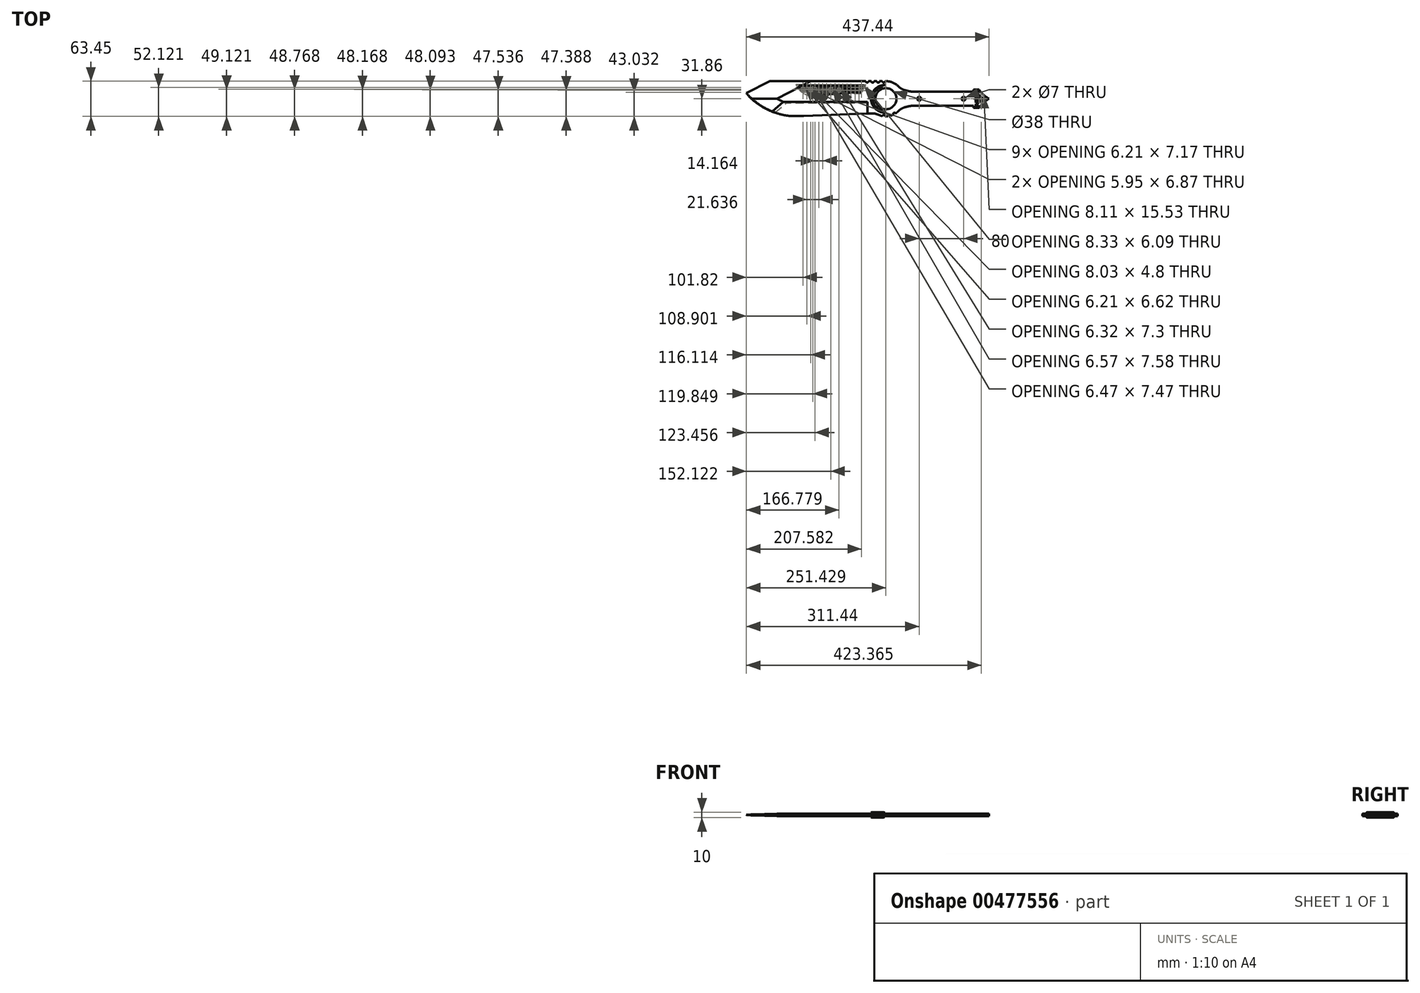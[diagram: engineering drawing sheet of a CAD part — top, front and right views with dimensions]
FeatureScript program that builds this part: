
annotation { "Feature Type Name" : "Feature", "Feature Type Description" : "" }
export const myFeature = defineFeature(function(context is Context, id is Id, definition is map)
    precondition{}
    {
        {
            var Q0;
            Q0=qCreatedBy(makeId("Top.planeOp"),FACE);
            var sketch = newSketch(context, id + "F0", { "sketchPlane" : qUnion([Q0])});
            skLineSegment(sketch, "E0", {"start": v(57.87, 16.75) * mm, "end": v(67.87, 16.75) * mm});
            skLineSegment(sketch, "E1", {"start": v(57.87, 16.75) * mm, "end": v(57.87, 12.5) * mm});
            skLineSegment(sketch, "E2", {"start": v(57.87, 12.5) * mm, "end": v(-46.76, 12.5) * mm});
            skArc(sketch, "E3", {"start": v(-67.13, 15.9) * mm, "mid": v(-57.09, 13.35) * mm, "end": v(-46.76, 12.5) * mm});
            skArc(sketch, "E4", {"start": v(-77.6, 22.42) * mm, "mid": v(-86.65, 28.75) * mm, "end": v(-97.34, 31.6) * mm});
            skCircle(sketch, "E5", {"center": v(-100.01, 0) * mm, "radius": 19 * mm});
            skLineSegment(sketch, "E6.MirrorCS", {"start": v(57.87, -16.75) * mm, "end": v(67.87, -16.75) * mm});
            skLineSegment(sketch, "E7.MirrorCS", {"start": v(57.87, -12.5) * mm, "end": v(57.87, -16.75) * mm});
            skLineSegment(sketch, "E8.MirrorCS", {"start": v(57.87, -12.5) * mm, "end": v(-46.76, -12.5) * mm});
            skArc(sketch, "E9.MirrorCS", {"start": v(-67.13, -15.9) * mm, "mid": v(-57.09, -13.35) * mm, "end": v(-46.76, -12.5) * mm});
            skArc(sketch, "E10.MirrorCS", {"start": v(-77.6, -22.42) * mm, "mid": v(-87.33, -29.06) * mm, "end": v(-98.81, -31.68) * mm});
            skPoint(sketch, "E11.visualSharp", {"position": v(-125.37, 19.03) * mm});
            skPoint(sketch, "E12.visualSharp", {"position": v(-125.37, -19.03) * mm});
            skPoint(sketch, "E13.visualSharp", {"position": v(-74.65, 19.03) * mm});
            skArc(sketch, "E13.filletArc", {"start": v(-77.6, 22.42) * mm, "mid": v(-72.73, 18.56) * mm, "end": v(-67.13, 15.9) * mm});
            skPoint(sketch, "E14.visualSharp", {"position": v(-74.65, -19.03) * mm});
            skArc(sketch, "E14.filletArc", {"start": v(-67.13, -15.9) * mm, "mid": v(-72.73, -18.56) * mm, "end": v(-77.6, -22.42) * mm});
            skLineSegment(sketch, "E15", {"start": v(-367.34, 31.6) * mm, "end": v(-97.34, 31.6) * mm});
            skArc(sketch, "E16", {"start": v(-112.05, -29.48) * mm, "mid": v(-105.6, -31.54) * mm, "end": v(-98.81, -31.68) * mm});
            skPoint(sketch, "E17.startSnap0", {"position": v(-107.38, -31.17) * mm});
            skPoint(sketch, "E18.visualSharp", {"position": v(-117.7, -25.6) * mm});
            skArc(sketch, "E18.filletArc", {"start": v(-112.05, -29.48) * mm, "mid": v(-119.77, -26.93) * mm, "end": v(-127.88, -26.55) * mm});
            skCircle(sketch, "E19", {"center": v(-103.96, 31.59) * mm, "radius": 2.5 * mm});
            skCircle(sketch, "E20", {"center": v(-84.58, -27.7) * mm, "radius": 2.5 * mm});
            skCircle(sketch, "E21", {"center": v(-93.98, -31.13) * mm, "radius": 2.5 * mm});
            skCircle(sketch, "E22", {"center": v(-103.96, -31.76) * mm, "radius": 2.5 * mm});
            skCircle(sketch, "E23", {"center": v(-113.96, 31.59) * mm, "radius": 2.5 * mm});
            skCircle(sketch, "E24", {"center": v(-123.96, 31.6) * mm, "radius": 2.5 * mm});
            skCircle(sketch, "E25", {"center": v(-133.96, 31.6) * mm, "radius": 2.5 * mm});
            skLineSegment(sketch, "E26", {"start": v(-267.3, 23.3) * mm, "end": v(-139.7, 23.3) * mm});
            skArc(sketch, "E27", {"start": v(-139.7, 23.3) * mm, "mid": v(-143.36, 18.11) * mm, "end": v(-144.92, 11.95) * mm});
            skArc(sketch, "E28", {"start": v(-267.3, 23.3) * mm, "mid": v(-239.83, 11.16) * mm, "end": v(-209.95, 8.17) * mm});
            skArc(sketch, "E29", {"start": v(-144.92, 11.95) * mm, "mid": v(-177.45, 10.33) * mm, "end": v(-209.95, 8.17) * mm});
            skCircle(sketch, "E30.cCircle", {"center": v(-144.92, 20.8) * mm, "radius": 3.1 * mm, "construction": true});
            skLineSegment(sketch, "E30.0", {"start": v(-141.81, 19.01) * mm, "end": v(-144.92, 17.22) * mm});
            skLineSegment(sketch, "E30.1", {"start": v(-144.92, 17.22) * mm, "end": v(-148.02, 19.01) * mm});
            skLineSegment(sketch, "E30.2", {"start": v(-148.02, 19.01) * mm, "end": v(-148.02, 22.6) * mm});
            skLineSegment(sketch, "E30.3", {"start": v(-148.02, 22.6) * mm, "end": v(-144.92, 24.4) * mm});
            skLineSegment(sketch, "E30.4", {"start": v(-144.92, 24.4) * mm, "end": v(-141.81, 22.6) * mm});
            skLineSegment(sketch, "E30.5", {"start": v(-141.81, 22.6) * mm, "end": v(-141.81, 19.01) * mm});
            skPoint(sketch, "E30.0.midPoint", {"position": v(-143.36, 18.11) * mm});
            skCircle(sketch, "E31.cCircle", {"center": v(-152.13, 20.95) * mm, "radius": 3.1 * mm, "construction": true});
            skPoint(sketch, "E31.cCircle.centerSnap0", {"position": v(-149.02, 20.95) * mm});
            skPoint(sketch, "E31.cCircle.perimeterSnap0", {"position": v(-148.02, 20.8) * mm});
            skLineSegment(sketch, "E31.0", {"start": v(-149.02, 22.75) * mm, "end": v(-149.02, 19.16) * mm});
            skLineSegment(sketch, "E31.1", {"start": v(-149.02, 19.16) * mm, "end": v(-152.13, 17.37) * mm});
            skLineSegment(sketch, "E31.2", {"start": v(-152.13, 17.37) * mm, "end": v(-155.23, 19.16) * mm});
            skLineSegment(sketch, "E31.3", {"start": v(-155.23, 19.16) * mm, "end": v(-155.23, 22.75) * mm});
            skLineSegment(sketch, "E31.4", {"start": v(-155.23, 22.75) * mm, "end": v(-152.13, 24.54) * mm});
            skLineSegment(sketch, "E31.5", {"start": v(-152.13, 24.54) * mm, "end": v(-149.02, 22.75) * mm});
            skPoint(sketch, "E31.0.midPoint", {"position": v(-149.02, 20.95) * mm});
            skPoint(sketch, "E31.0.midPoint.positionSnap0", {"position": v(-149.02, 20.95) * mm});
            skCircle(sketch, "E32.cCircle", {"center": v(-159.34, 21.05) * mm, "radius": 3.1 * mm, "construction": true});
            skLineSegment(sketch, "E32.0", {"start": v(-156.23, 22.85) * mm, "end": v(-156.23, 19.26) * mm});
            skLineSegment(sketch, "E32.1", {"start": v(-156.23, 19.26) * mm, "end": v(-159.34, 17.47) * mm});
            skLineSegment(sketch, "E32.2", {"start": v(-159.34, 17.47) * mm, "end": v(-162.45, 19.26) * mm});
            skLineSegment(sketch, "E32.3", {"start": v(-162.45, 19.26) * mm, "end": v(-162.45, 22.85) * mm});
            skLineSegment(sketch, "E32.4", {"start": v(-162.45, 22.85) * mm, "end": v(-159.34, 24.64) * mm});
            skLineSegment(sketch, "E32.5", {"start": v(-159.34, 24.64) * mm, "end": v(-156.23, 22.85) * mm});
            skCircle(sketch, "E33.cCircle", {"center": v(-166.55, 21.2) * mm, "radius": 3.1 * mm, "construction": true});
            skLineSegment(sketch, "E33.0", {"start": v(-163.45, 23) * mm, "end": v(-163.45, 19.41) * mm});
            skLineSegment(sketch, "E33.1", {"start": v(-163.45, 19.41) * mm, "end": v(-166.55, 17.62) * mm});
            skLineSegment(sketch, "E33.2", {"start": v(-166.55, 17.62) * mm, "end": v(-169.66, 19.41) * mm});
            skLineSegment(sketch, "E33.3", {"start": v(-169.66, 19.41) * mm, "end": v(-169.66, 23) * mm});
            skLineSegment(sketch, "E33.4", {"start": v(-169.66, 23) * mm, "end": v(-166.55, 24.8) * mm});
            skLineSegment(sketch, "E33.5", {"start": v(-166.55, 24.8) * mm, "end": v(-163.45, 23) * mm});
            skCircle(sketch, "E34.cCircle", {"center": v(-173.76, 21.35) * mm, "radius": 3.1 * mm, "construction": true});
            skLineSegment(sketch, "E34.0", {"start": v(-170.66, 23.15) * mm, "end": v(-170.66, 19.56) * mm});
            skLineSegment(sketch, "E34.1", {"start": v(-170.66, 19.56) * mm, "end": v(-173.76, 17.77) * mm});
            skLineSegment(sketch, "E34.2", {"start": v(-173.76, 17.77) * mm, "end": v(-176.87, 19.56) * mm});
            skLineSegment(sketch, "E34.3", {"start": v(-176.87, 19.56) * mm, "end": v(-176.87, 23.15) * mm});
            skLineSegment(sketch, "E34.4", {"start": v(-176.87, 23.15) * mm, "end": v(-173.76, 24.94) * mm});
            skLineSegment(sketch, "E34.5", {"start": v(-173.76, 24.94) * mm, "end": v(-170.66, 23.15) * mm});
            skCircle(sketch, "E35.cCircle", {"center": v(-180.98, 21.5) * mm, "radius": 3.1 * mm, "construction": true});
            skLineSegment(sketch, "E35.0", {"start": v(-177.87, 19.71) * mm, "end": v(-180.98, 17.92) * mm});
            skLineSegment(sketch, "E35.1", {"start": v(-180.98, 17.92) * mm, "end": v(-184.08, 19.71) * mm});
            skLineSegment(sketch, "E35.2", {"start": v(-184.08, 19.71) * mm, "end": v(-184.08, 23.3) * mm});
            skLineSegment(sketch, "E35.3", {"start": v(-184.08, 23.3) * mm, "end": v(-180.98, 25.1) * mm});
            skLineSegment(sketch, "E35.4", {"start": v(-180.98, 25.1) * mm, "end": v(-177.87, 23.3) * mm});
            skLineSegment(sketch, "E35.5", {"start": v(-177.87, 23.3) * mm, "end": v(-177.87, 19.71) * mm});
            skPoint(sketch, "E35.0.midPoint", {"position": v(-179.42, 18.81) * mm});
            skCircle(sketch, "E36.cCircle", {"center": v(-188.19, 21.65) * mm, "radius": 3.1 * mm, "construction": true});
            skLineSegment(sketch, "E36.0", {"start": v(-185.08, 23.45) * mm, "end": v(-185.08, 19.86) * mm});
            skLineSegment(sketch, "E36.1", {"start": v(-185.08, 19.86) * mm, "end": v(-188.19, 18.07) * mm});
            skLineSegment(sketch, "E36.2", {"start": v(-188.19, 18.07) * mm, "end": v(-191.3, 19.86) * mm});
            skLineSegment(sketch, "E36.3", {"start": v(-191.3, 19.86) * mm, "end": v(-191.3, 23.45) * mm});
            skLineSegment(sketch, "E36.4", {"start": v(-191.3, 23.45) * mm, "end": v(-188.19, 25.24) * mm});
            skLineSegment(sketch, "E36.5", {"start": v(-188.19, 25.24) * mm, "end": v(-185.08, 23.45) * mm});
            skCircle(sketch, "E37.cCircle", {"center": v(-195.4, 21.8) * mm, "radius": 3.1 * mm, "construction": true});
            skLineSegment(sketch, "E37.0", {"start": v(-192.3, 23.6) * mm, "end": v(-192.3, 20.01) * mm});
            skLineSegment(sketch, "E37.1", {"start": v(-192.3, 20.01) * mm, "end": v(-195.4, 18.22) * mm});
            skLineSegment(sketch, "E37.2", {"start": v(-195.4, 18.22) * mm, "end": v(-198.5, 20.01) * mm});
            skLineSegment(sketch, "E37.3", {"start": v(-198.5, 20.01) * mm, "end": v(-198.5, 23.6) * mm});
            skLineSegment(sketch, "E37.4", {"start": v(-198.5, 23.6) * mm, "end": v(-195.4, 25.4) * mm});
            skLineSegment(sketch, "E37.5", {"start": v(-195.4, 25.4) * mm, "end": v(-192.3, 23.6) * mm});
            skCircle(sketch, "E38.cCircle", {"center": v(-202.61, 21.95) * mm, "radius": 3.1 * mm, "construction": true});
            skLineSegment(sketch, "E38.0", {"start": v(-199.5, 23.75) * mm, "end": v(-199.5, 20.16) * mm});
            skLineSegment(sketch, "E38.1", {"start": v(-199.5, 20.16) * mm, "end": v(-202.61, 18.37) * mm});
            skLineSegment(sketch, "E38.2", {"start": v(-202.61, 18.37) * mm, "end": v(-205.72, 20.16) * mm});
            skLineSegment(sketch, "E38.3", {"start": v(-205.72, 20.16) * mm, "end": v(-205.72, 23.75) * mm});
            skLineSegment(sketch, "E38.4", {"start": v(-205.72, 23.75) * mm, "end": v(-202.61, 25.54) * mm});
            skLineSegment(sketch, "E38.5", {"start": v(-202.61, 25.54) * mm, "end": v(-199.5, 23.75) * mm});
            skCircle(sketch, "E39.cCircle", {"center": v(-217.04, 22.1) * mm, "radius": 3.1 * mm, "construction": true});
            skLineSegment(sketch, "E39.0", {"start": v(-213.93, 23.9) * mm, "end": v(-213.93, 20.31) * mm});
            skLineSegment(sketch, "E39.1", {"start": v(-213.93, 20.31) * mm, "end": v(-217.04, 18.52) * mm});
            skLineSegment(sketch, "E39.2", {"start": v(-217.04, 18.52) * mm, "end": v(-220.14, 20.31) * mm});
            skLineSegment(sketch, "E39.3", {"start": v(-220.14, 20.31) * mm, "end": v(-220.14, 23.9) * mm});
            skLineSegment(sketch, "E39.4", {"start": v(-220.14, 23.9) * mm, "end": v(-217.04, 25.7) * mm});
            skLineSegment(sketch, "E39.5", {"start": v(-217.04, 25.7) * mm, "end": v(-213.93, 23.9) * mm});
            skPoint(sketch, "E40", {"position": v(-220.14, 22.1) * mm});
            skCircle(sketch, "E41.cCircle", {"center": v(-209.82, 22.25) * mm, "radius": 3.1 * mm, "construction": true});
            skLineSegment(sketch, "E41.0", {"start": v(-206.72, 24.05) * mm, "end": v(-206.72, 20.46) * mm});
            skLineSegment(sketch, "E41.1", {"start": v(-206.72, 20.46) * mm, "end": v(-209.82, 18.67) * mm});
            skLineSegment(sketch, "E41.2", {"start": v(-209.82, 18.67) * mm, "end": v(-212.93, 20.46) * mm});
            skLineSegment(sketch, "E41.3", {"start": v(-212.93, 20.46) * mm, "end": v(-212.93, 24.05) * mm});
            skLineSegment(sketch, "E41.4", {"start": v(-212.93, 24.05) * mm, "end": v(-209.82, 25.84) * mm});
            skLineSegment(sketch, "E41.5", {"start": v(-209.82, 25.84) * mm, "end": v(-206.72, 24.05) * mm});
            skCircle(sketch, "E42.cCircle", {"center": v(-224.25, 22.4) * mm, "radius": 3.1 * mm, "construction": true});
            skLineSegment(sketch, "E42.0", {"start": v(-221.14, 24.2) * mm, "end": v(-221.14, 20.61) * mm});
            skLineSegment(sketch, "E42.1", {"start": v(-221.14, 20.61) * mm, "end": v(-224.25, 18.82) * mm});
            skLineSegment(sketch, "E42.2", {"start": v(-224.25, 18.82) * mm, "end": v(-227.35, 20.61) * mm});
            skLineSegment(sketch, "E42.3", {"start": v(-227.35, 20.61) * mm, "end": v(-227.35, 24.2) * mm});
            skLineSegment(sketch, "E42.4", {"start": v(-227.35, 24.2) * mm, "end": v(-224.25, 26) * mm});
            skLineSegment(sketch, "E42.5", {"start": v(-224.25, 26) * mm, "end": v(-221.14, 24.2) * mm});
            skCircle(sketch, "E43.cCircle", {"center": v(-231.46, 22.55) * mm, "radius": 3.1 * mm, "construction": true});
            skLineSegment(sketch, "E43.0", {"start": v(-228.35, 24.35) * mm, "end": v(-228.35, 20.76) * mm});
            skLineSegment(sketch, "E43.1", {"start": v(-228.35, 20.76) * mm, "end": v(-231.46, 18.97) * mm});
            skLineSegment(sketch, "E43.2", {"start": v(-231.46, 18.97) * mm, "end": v(-234.57, 20.76) * mm});
            skLineSegment(sketch, "E43.3", {"start": v(-234.57, 20.76) * mm, "end": v(-234.57, 24.35) * mm});
            skLineSegment(sketch, "E43.4", {"start": v(-234.57, 24.35) * mm, "end": v(-231.46, 26.14) * mm});
            skLineSegment(sketch, "E43.5", {"start": v(-231.46, 26.14) * mm, "end": v(-228.35, 24.35) * mm});
            skCircle(sketch, "E44.cCircle", {"center": v(-238.67, 22.85) * mm, "radius": 3.1 * mm, "construction": true});
            skLineSegment(sketch, "E44.0", {"start": v(-235.57, 24.65) * mm, "end": v(-235.57, 21.06) * mm});
            skLineSegment(sketch, "E44.1", {"start": v(-235.57, 21.06) * mm, "end": v(-238.67, 19.27) * mm});
            skLineSegment(sketch, "E44.2", {"start": v(-238.67, 19.27) * mm, "end": v(-241.78, 21.06) * mm});
            skLineSegment(sketch, "E44.3", {"start": v(-241.78, 21.06) * mm, "end": v(-241.78, 24.65) * mm});
            skLineSegment(sketch, "E44.4", {"start": v(-241.78, 24.65) * mm, "end": v(-238.67, 26.44) * mm});
            skLineSegment(sketch, "E44.5", {"start": v(-238.67, 26.44) * mm, "end": v(-235.57, 24.65) * mm});
            skCircle(sketch, "E45.cCircle", {"center": v(-245.88, 23.15) * mm, "radius": 3.1 * mm, "construction": true});
            skLineSegment(sketch, "E45.0", {"start": v(-242.78, 24.95) * mm, "end": v(-242.78, 21.36) * mm});
            skLineSegment(sketch, "E45.1", {"start": v(-242.78, 21.36) * mm, "end": v(-245.88, 19.57) * mm});
            skLineSegment(sketch, "E45.2", {"start": v(-245.88, 19.57) * mm, "end": v(-249, 21.36) * mm});
            skLineSegment(sketch, "E45.3", {"start": v(-249, 21.36) * mm, "end": v(-249, 24.95) * mm});
            skLineSegment(sketch, "E45.4", {"start": v(-249, 24.95) * mm, "end": v(-245.88, 26.74) * mm});
            skLineSegment(sketch, "E45.5", {"start": v(-245.88, 26.74) * mm, "end": v(-242.78, 24.95) * mm});
            skCircle(sketch, "E46.cCircle", {"center": v(-253.1, 23.3) * mm, "radius": 3.1 * mm, "construction": true});
            skLineSegment(sketch, "E46.0", {"start": v(-250, 25.1) * mm, "end": v(-250, 21.51) * mm});
            skLineSegment(sketch, "E46.1", {"start": v(-250, 21.51) * mm, "end": v(-253.1, 19.72) * mm});
            skLineSegment(sketch, "E46.2", {"start": v(-253.1, 19.72) * mm, "end": v(-256.2, 21.51) * mm});
            skLineSegment(sketch, "E46.3", {"start": v(-256.2, 21.51) * mm, "end": v(-256.2, 25.1) * mm});
            skLineSegment(sketch, "E46.4", {"start": v(-256.2, 25.1) * mm, "end": v(-253.1, 26.9) * mm});
            skLineSegment(sketch, "E46.5", {"start": v(-253.1, 26.9) * mm, "end": v(-250, 25.1) * mm});
            skCircle(sketch, "E47.cCircle", {"center": v(-235.33, 16.3) * mm, "radius": 3.24 * mm, "construction": true});
            skLineSegment(sketch, "E47.0", {"start": v(-232.1, 18.18) * mm, "end": v(-232.1, 14.44) * mm});
            skLineSegment(sketch, "E47.1", {"start": v(-232.1, 14.44) * mm, "end": v(-235.33, 12.57) * mm});
            skLineSegment(sketch, "E47.2", {"start": v(-235.33, 12.57) * mm, "end": v(-238.56, 14.44) * mm});
            skLineSegment(sketch, "E47.3", {"start": v(-238.56, 14.44) * mm, "end": v(-238.56, 18.18) * mm});
            skLineSegment(sketch, "E47.4", {"start": v(-238.56, 18.18) * mm, "end": v(-235.33, 20.04) * mm});
            skLineSegment(sketch, "E47.5", {"start": v(-235.33, 20.04) * mm, "end": v(-232.1, 18.18) * mm});
            skCircle(sketch, "E48.cCircle", {"center": v(-227.98, 16.23) * mm, "radius": 3.1 * mm, "construction": true});
            skLineSegment(sketch, "E48.0", {"start": v(-224.88, 18.03) * mm, "end": v(-224.88, 14.44) * mm});
            skLineSegment(sketch, "E48.1", {"start": v(-224.88, 14.44) * mm, "end": v(-227.98, 12.65) * mm});
            skLineSegment(sketch, "E48.2", {"start": v(-227.98, 12.65) * mm, "end": v(-231.1, 14.44) * mm});
            skLineSegment(sketch, "E48.3", {"start": v(-231.1, 14.44) * mm, "end": v(-231.1, 18.03) * mm});
            skLineSegment(sketch, "E48.4", {"start": v(-231.1, 18.03) * mm, "end": v(-227.98, 19.82) * mm});
            skLineSegment(sketch, "E48.5", {"start": v(-227.98, 19.82) * mm, "end": v(-224.88, 18.03) * mm});
            skCircle(sketch, "E49.cCircle", {"center": v(-191.93, 15.8) * mm, "radius": 3.1 * mm, "construction": true});
            skLineSegment(sketch, "E49.0", {"start": v(-188.82, 17.59) * mm, "end": v(-188.82, 14) * mm});
            skLineSegment(sketch, "E49.1", {"start": v(-188.82, 14) * mm, "end": v(-191.93, 12.2) * mm});
            skLineSegment(sketch, "E49.2", {"start": v(-191.93, 12.2) * mm, "end": v(-195.03, 14) * mm});
            skLineSegment(sketch, "E49.3", {"start": v(-195.03, 14) * mm, "end": v(-195.03, 17.59) * mm});
            skLineSegment(sketch, "E49.4", {"start": v(-195.03, 17.59) * mm, "end": v(-191.93, 19.38) * mm});
            skLineSegment(sketch, "E49.5", {"start": v(-191.93, 19.38) * mm, "end": v(-188.82, 17.59) * mm});
            skCircle(sketch, "E50.cCircle", {"center": v(-249.62, 16.98) * mm, "radius": 3.1 * mm, "construction": true});
            skLineSegment(sketch, "E50.0", {"start": v(-246.51, 18.78) * mm, "end": v(-246.51, 15.19) * mm});
            skLineSegment(sketch, "E50.1", {"start": v(-246.51, 15.19) * mm, "end": v(-249.62, 13.4) * mm});
            skLineSegment(sketch, "E50.2", {"start": v(-249.62, 13.4) * mm, "end": v(-252.74, 15.2) * mm});
            skLineSegment(sketch, "E50.3", {"start": v(-252.73, 15.19) * mm, "end": v(-252.73, 18.78) * mm});
            skLineSegment(sketch, "E50.4", {"start": v(-252.73, 18.78) * mm, "end": v(-249.62, 20.57) * mm});
            skLineSegment(sketch, "E50.5", {"start": v(-249.62, 20.57) * mm, "end": v(-246.51, 18.78) * mm});
            skCircle(sketch, "E51.cCircle", {"center": v(-242.54, 16.9) * mm, "radius": 2.98 * mm, "construction": true});
            skLineSegment(sketch, "E51.0", {"start": v(-239.56, 18.63) * mm, "end": v(-239.56, 15.19) * mm});
            skLineSegment(sketch, "E51.1", {"start": v(-239.56, 15.19) * mm, "end": v(-242.54, 13.47) * mm});
            skLineSegment(sketch, "E51.2", {"start": v(-242.54, 13.47) * mm, "end": v(-245.51, 15.19) * mm});
            skLineSegment(sketch, "E51.3", {"start": v(-245.51, 15.19) * mm, "end": v(-245.51, 18.63) * mm});
            skLineSegment(sketch, "E51.4", {"start": v(-245.51, 18.63) * mm, "end": v(-242.54, 20.34) * mm});
            skLineSegment(sketch, "E51.5", {"start": v(-242.54, 20.34) * mm, "end": v(-239.56, 18.63) * mm});
            skCircle(sketch, "E52.cCircle", {"center": v(-177.4, 15.3) * mm, "radius": 3.1 * mm, "construction": true});
            skLineSegment(sketch, "E52.0", {"start": v(-174.29, 17.1) * mm, "end": v(-174.29, 13.51) * mm});
            skLineSegment(sketch, "E52.1", {"start": v(-174.29, 13.51) * mm, "end": v(-177.4, 11.72) * mm});
            skLineSegment(sketch, "E52.2", {"start": v(-177.4, 11.72) * mm, "end": v(-180.5, 13.51) * mm});
            skLineSegment(sketch, "E52.3", {"start": v(-180.5, 13.51) * mm, "end": v(-180.5, 17.1) * mm});
            skLineSegment(sketch, "E52.4", {"start": v(-180.5, 17.1) * mm, "end": v(-177.4, 18.9) * mm});
            skLineSegment(sketch, "E52.5", {"start": v(-177.4, 18.9) * mm, "end": v(-174.29, 17.1) * mm});
            skCircle(sketch, "E53.cCircle", {"center": v(-220.9, 16.16) * mm, "radius": 2.98 * mm, "construction": true});
            skLineSegment(sketch, "E53.0", {"start": v(-217.93, 17.88) * mm, "end": v(-217.93, 14.44) * mm});
            skLineSegment(sketch, "E53.1", {"start": v(-217.93, 14.44) * mm, "end": v(-220.9, 12.72) * mm});
            skLineSegment(sketch, "E53.2", {"start": v(-220.9, 12.72) * mm, "end": v(-223.88, 14.44) * mm});
            skLineSegment(sketch, "E53.3", {"start": v(-223.88, 14.44) * mm, "end": v(-223.88, 17.88) * mm});
            skLineSegment(sketch, "E53.4", {"start": v(-223.88, 17.88) * mm, "end": v(-220.9, 19.6) * mm});
            skLineSegment(sketch, "E53.5", {"start": v(-220.9, 19.6) * mm, "end": v(-217.93, 17.88) * mm});
            skCircle(sketch, "E54.cCircle", {"center": v(-213.82, 16.35) * mm, "radius": 3.1 * mm, "construction": true});
            skLineSegment(sketch, "E54.0", {"start": v(-210.71, 18.15) * mm, "end": v(-210.71, 14.56) * mm});
            skLineSegment(sketch, "E54.1", {"start": v(-210.71, 14.56) * mm, "end": v(-213.82, 12.77) * mm});
            skLineSegment(sketch, "E54.2", {"start": v(-213.82, 12.77) * mm, "end": v(-216.93, 14.56) * mm});
            skLineSegment(sketch, "E54.3", {"start": v(-216.93, 14.56) * mm, "end": v(-216.93, 18.15) * mm});
            skLineSegment(sketch, "E54.4", {"start": v(-216.93, 18.15) * mm, "end": v(-213.82, 19.94) * mm});
            skLineSegment(sketch, "E54.5", {"start": v(-213.82, 19.94) * mm, "end": v(-210.71, 18.15) * mm});
            skCircle(sketch, "E55.cCircle", {"center": v(-206.6, 15.93) * mm, "radius": 3.1 * mm, "construction": true});
            skLineSegment(sketch, "E55.0", {"start": v(-203.5, 17.73) * mm, "end": v(-203.5, 14.14) * mm});
            skLineSegment(sketch, "E55.1", {"start": v(-203.5, 14.14) * mm, "end": v(-206.6, 12.35) * mm});
            skLineSegment(sketch, "E55.2", {"start": v(-206.6, 12.35) * mm, "end": v(-209.71, 14.14) * mm});
            skLineSegment(sketch, "E55.3", {"start": v(-209.71, 14.14) * mm, "end": v(-209.71, 17.73) * mm});
            skLineSegment(sketch, "E55.4", {"start": v(-209.71, 17.73) * mm, "end": v(-206.6, 19.52) * mm});
            skLineSegment(sketch, "E55.5", {"start": v(-206.6, 19.52) * mm, "end": v(-203.5, 17.73) * mm});
            skCircle(sketch, "E56.cCircle", {"center": v(-199.32, 15.68) * mm, "radius": 3.28 * mm, "construction": true});
            skLineSegment(sketch, "E56.0", {"start": v(-196.03, 17.57) * mm, "end": v(-196.03, 13.78) * mm});
            skLineSegment(sketch, "E56.1", {"start": v(-196.03, 13.78) * mm, "end": v(-199.32, 11.88) * mm});
            skLineSegment(sketch, "E56.2", {"start": v(-199.32, 11.88) * mm, "end": v(-202.6, 13.78) * mm});
            skLineSegment(sketch, "E56.3", {"start": v(-202.6, 13.78) * mm, "end": v(-202.6, 17.57) * mm});
            skLineSegment(sketch, "E56.4", {"start": v(-202.6, 17.57) * mm, "end": v(-199.32, 19.47) * mm});
            skLineSegment(sketch, "E56.5", {"start": v(-199.32, 19.47) * mm, "end": v(-196.03, 17.57) * mm});
            skCircle(sketch, "E57.cCircle", {"center": v(-184.66, 15.53) * mm, "radius": 3.16 * mm, "construction": true});
            skLineSegment(sketch, "E57.0", {"start": v(-181.5, 17.35) * mm, "end": v(-181.5, 13.7) * mm});
            skLineSegment(sketch, "E57.1", {"start": v(-181.5, 13.7) * mm, "end": v(-184.66, 11.88) * mm});
            skLineSegment(sketch, "E57.2", {"start": v(-184.66, 11.88) * mm, "end": v(-187.82, 13.7) * mm});
            skLineSegment(sketch, "E57.3", {"start": v(-187.82, 13.7) * mm, "end": v(-187.82, 17.35) * mm});
            skLineSegment(sketch, "E57.4", {"start": v(-187.82, 17.35) * mm, "end": v(-184.66, 19.18) * mm});
            skLineSegment(sketch, "E57.5", {"start": v(-184.66, 19.18) * mm, "end": v(-181.5, 17.35) * mm});
            skCircle(sketch, "E58.cCircle", {"center": v(-170.18, 15.19) * mm, "radius": 3.1 * mm, "construction": true});
            skLineSegment(sketch, "E58.0", {"start": v(-167.08, 16.98) * mm, "end": v(-167.08, 13.4) * mm});
            skLineSegment(sketch, "E58.1", {"start": v(-167.08, 13.4) * mm, "end": v(-170.18, 11.6) * mm});
            skLineSegment(sketch, "E58.2", {"start": v(-170.18, 11.6) * mm, "end": v(-173.29, 13.4) * mm});
            skLineSegment(sketch, "E58.3", {"start": v(-173.29, 13.4) * mm, "end": v(-173.29, 16.98) * mm});
            skLineSegment(sketch, "E58.4", {"start": v(-173.29, 16.98) * mm, "end": v(-170.18, 18.78) * mm});
            skLineSegment(sketch, "E58.5", {"start": v(-170.18, 18.78) * mm, "end": v(-167.08, 16.98) * mm});
            skCircle(sketch, "E59.cCircle", {"center": v(-162.97, 15.19) * mm, "radius": 3.1 * mm, "construction": true});
            skLineSegment(sketch, "E59.0", {"start": v(-159.86, 16.98) * mm, "end": v(-159.86, 13.4) * mm});
            skLineSegment(sketch, "E59.1", {"start": v(-159.86, 13.4) * mm, "end": v(-162.97, 11.6) * mm});
            skLineSegment(sketch, "E59.2", {"start": v(-162.97, 11.6) * mm, "end": v(-166.08, 13.4) * mm});
            skLineSegment(sketch, "E59.3", {"start": v(-166.08, 13.4) * mm, "end": v(-166.08, 16.98) * mm});
            skLineSegment(sketch, "E59.4", {"start": v(-166.08, 16.98) * mm, "end": v(-162.97, 18.78) * mm});
            skLineSegment(sketch, "E59.5", {"start": v(-162.97, 18.78) * mm, "end": v(-159.86, 16.98) * mm});
            skCircle(sketch, "E60.cCircle", {"center": v(-155.76, 14.98) * mm, "radius": 3.1 * mm, "construction": true});
            skLineSegment(sketch, "E60.0", {"start": v(-152.65, 16.77) * mm, "end": v(-152.65, 13.19) * mm});
            skLineSegment(sketch, "E60.1", {"start": v(-152.65, 13.19) * mm, "end": v(-155.76, 11.4) * mm});
            skLineSegment(sketch, "E60.2", {"start": v(-155.76, 11.4) * mm, "end": v(-158.86, 13.19) * mm});
            skLineSegment(sketch, "E60.3", {"start": v(-158.86, 13.19) * mm, "end": v(-158.86, 16.77) * mm});
            skLineSegment(sketch, "E60.4", {"start": v(-158.86, 16.77) * mm, "end": v(-155.76, 18.57) * mm});
            skLineSegment(sketch, "E60.5", {"start": v(-155.76, 18.57) * mm, "end": v(-152.65, 16.77) * mm});
            skCircle(sketch, "E61.cCircle", {"center": v(-148.54, 14.7) * mm, "radius": 3.1 * mm, "construction": true});
            skLineSegment(sketch, "E61.0", {"start": v(-145.44, 16.49) * mm, "end": v(-145.44, 12.9) * mm});
            skLineSegment(sketch, "E61.1", {"start": v(-145.44, 12.9) * mm, "end": v(-148.54, 11.1) * mm});
            skLineSegment(sketch, "E61.2", {"start": v(-148.54, 11.1) * mm, "end": v(-151.65, 12.9) * mm});
            skLineSegment(sketch, "E61.3", {"start": v(-151.65, 12.9) * mm, "end": v(-151.65, 16.49) * mm});
            skLineSegment(sketch, "E61.4", {"start": v(-151.65, 16.49) * mm, "end": v(-148.54, 18.28) * mm});
            skLineSegment(sketch, "E61.5", {"start": v(-148.54, 18.28) * mm, "end": v(-145.44, 16.49) * mm});
            skCircle(sketch, "E62.cCircle", {"center": v(-239.71, 10.36) * mm, "radius": 3.1 * mm, "construction": true});
            skLineSegment(sketch, "E62.0", {"start": v(-236.6, 12.16) * mm, "end": v(-236.6, 8.57) * mm});
            skLineSegment(sketch, "E62.1", {"start": v(-236.6, 8.57) * mm, "end": v(-239.71, 6.78) * mm});
            skLineSegment(sketch, "E62.2", {"start": v(-239.71, 6.78) * mm, "end": v(-242.82, 8.57) * mm});
            skLineSegment(sketch, "E62.3", {"start": v(-242.82, 8.57) * mm, "end": v(-242.82, 12.16) * mm});
            skLineSegment(sketch, "E62.4", {"start": v(-242.82, 12.16) * mm, "end": v(-239.71, 13.95) * mm});
            skLineSegment(sketch, "E62.5", {"start": v(-239.71, 13.95) * mm, "end": v(-236.6, 12.16) * mm});
            skCircle(sketch, "E63.cCircle", {"center": v(-231.6, 8.94) * mm, "radius": 4.02 * mm, "construction": true});
            skLineSegment(sketch, "E63.0", {"start": v(-227.58, 11.26) * mm, "end": v(-227.58, 6.62) * mm});
            skLineSegment(sketch, "E63.1", {"start": v(-227.58, 6.62) * mm, "end": v(-231.6, 4.3) * mm});
            skLineSegment(sketch, "E63.2", {"start": v(-231.6, 4.3) * mm, "end": v(-235.6, 6.62) * mm});
            skLineSegment(sketch, "E63.3", {"start": v(-235.6, 6.62) * mm, "end": v(-235.6, 11.26) * mm});
            skLineSegment(sketch, "E63.4", {"start": v(-235.6, 11.26) * mm, "end": v(-231.6, 13.57) * mm});
            skLineSegment(sketch, "E63.5", {"start": v(-231.6, 13.57) * mm, "end": v(-227.58, 11.26) * mm});
            skCircle(sketch, "E64.cCircle", {"center": v(-224.13, 10.02) * mm, "radius": 2.45 * mm, "construction": true});
            skLineSegment(sketch, "E64.0", {"start": v(-221.69, 11.43) * mm, "end": v(-221.69, 8.61) * mm});
            skLineSegment(sketch, "E64.1", {"start": v(-221.69, 8.61) * mm, "end": v(-224.13, 7.2) * mm});
            skLineSegment(sketch, "E64.2", {"start": v(-224.13, 7.2) * mm, "end": v(-226.58, 8.61) * mm});
            skLineSegment(sketch, "E64.3", {"start": v(-226.58, 8.61) * mm, "end": v(-226.58, 11.43) * mm});
            skLineSegment(sketch, "E64.4", {"start": v(-226.58, 11.43) * mm, "end": v(-224.13, 12.85) * mm});
            skLineSegment(sketch, "E64.5", {"start": v(-224.13, 12.85) * mm, "end": v(-221.69, 11.43) * mm});
            skCircle(sketch, "E65.cCircle", {"center": v(-217.58, 9.94) * mm, "radius": 3.1 * mm, "construction": true});
            skLineSegment(sketch, "E65.0", {"start": v(-214.47, 11.74) * mm, "end": v(-214.47, 8.15) * mm});
            skLineSegment(sketch, "E65.1", {"start": v(-214.47, 8.15) * mm, "end": v(-217.58, 6.35) * mm});
            skLineSegment(sketch, "E65.2", {"start": v(-217.58, 6.35) * mm, "end": v(-220.69, 8.15) * mm});
            skLineSegment(sketch, "E65.3", {"start": v(-220.69, 8.15) * mm, "end": v(-220.69, 11.74) * mm});
            skLineSegment(sketch, "E65.4", {"start": v(-220.69, 11.74) * mm, "end": v(-217.58, 13.53) * mm});
            skLineSegment(sketch, "E65.5", {"start": v(-217.58, 13.53) * mm, "end": v(-214.47, 11.74) * mm});
            skCircle(sketch, "E66.cCircle", {"center": v(-210.36, 9.82) * mm, "radius": 3.1 * mm, "construction": true});
            skLineSegment(sketch, "E66.0", {"start": v(-207.26, 11.62) * mm, "end": v(-207.26, 8.03) * mm});
            skLineSegment(sketch, "E66.1", {"start": v(-207.26, 8.03) * mm, "end": v(-210.36, 6.24) * mm});
            skLineSegment(sketch, "E66.2", {"start": v(-210.36, 6.24) * mm, "end": v(-213.47, 8.03) * mm});
            skLineSegment(sketch, "E66.3", {"start": v(-213.47, 8.03) * mm, "end": v(-213.47, 11.62) * mm});
            skLineSegment(sketch, "E66.4", {"start": v(-213.47, 11.62) * mm, "end": v(-210.36, 13.41) * mm});
            skLineSegment(sketch, "E66.5", {"start": v(-210.36, 13.41) * mm, "end": v(-207.26, 11.62) * mm});
            skCircle(sketch, "E67.cCircle", {"center": v(-203.1, 9.68) * mm, "radius": 3.16 * mm, "construction": true});
            skLineSegment(sketch, "E67.0", {"start": v(-199.94, 11.5) * mm, "end": v(-199.94, 7.86) * mm});
            skLineSegment(sketch, "E67.1", {"start": v(-199.94, 7.86) * mm, "end": v(-203.1, 6.03) * mm});
            skLineSegment(sketch, "E67.2", {"start": v(-203.1, 6.03) * mm, "end": v(-206.26, 7.86) * mm});
            skLineSegment(sketch, "E67.3", {"start": v(-206.26, 7.86) * mm, "end": v(-206.26, 11.5) * mm});
            skLineSegment(sketch, "E67.4", {"start": v(-206.26, 11.5) * mm, "end": v(-203.1, 13.33) * mm});
            skLineSegment(sketch, "E67.5", {"start": v(-203.1, 13.33) * mm, "end": v(-199.94, 11.5) * mm});
            skCircle(sketch, "E68.cCircle", {"center": v(-195.7, 9.2) * mm, "radius": 3.23 * mm, "construction": true});
            skLineSegment(sketch, "E68.0", {"start": v(-192.48, 11.07) * mm, "end": v(-192.48, 7.34) * mm});
            skLineSegment(sketch, "E68.1", {"start": v(-192.48, 7.34) * mm, "end": v(-195.7, 5.48) * mm});
            skLineSegment(sketch, "E68.2", {"start": v(-195.7, 5.48) * mm, "end": v(-198.94, 7.34) * mm});
            skLineSegment(sketch, "E68.3", {"start": v(-198.94, 7.34) * mm, "end": v(-198.94, 11.07) * mm});
            skLineSegment(sketch, "E68.4", {"start": v(-198.94, 11.07) * mm, "end": v(-195.7, 12.93) * mm});
            skLineSegment(sketch, "E68.5", {"start": v(-195.7, 12.93) * mm, "end": v(-192.48, 11.07) * mm});
            skCircle(sketch, "E69.cCircle", {"center": v(-188.2, 9.3) * mm, "radius": 3.29 * mm, "construction": true});
            skLineSegment(sketch, "E69.0", {"start": v(-184.9, 11.2) * mm, "end": v(-184.9, 7.4) * mm});
            skLineSegment(sketch, "E69.1", {"start": v(-184.9, 7.4) * mm, "end": v(-188.2, 5.5) * mm});
            skLineSegment(sketch, "E69.2", {"start": v(-188.2, 5.5) * mm, "end": v(-191.48, 7.4) * mm});
            skLineSegment(sketch, "E69.3", {"start": v(-191.48, 7.4) * mm, "end": v(-191.48, 11.2) * mm});
            skLineSegment(sketch, "E69.4", {"start": v(-191.48, 11.2) * mm, "end": v(-188.2, 13.1) * mm});
            skLineSegment(sketch, "E69.5", {"start": v(-188.2, 13.1) * mm, "end": v(-184.9, 11.2) * mm});
            skCircle(sketch, "E70.cCircle", {"center": v(-180.8, 9.41) * mm, "radius": 3.1 * mm, "construction": true});
            skLineSegment(sketch, "E70.0", {"start": v(-177.7, 11.2) * mm, "end": v(-177.7, 7.62) * mm});
            skLineSegment(sketch, "E70.1", {"start": v(-177.7, 7.62) * mm, "end": v(-180.8, 5.83) * mm});
            skLineSegment(sketch, "E70.2", {"start": v(-180.8, 5.83) * mm, "end": v(-183.9, 7.62) * mm});
            skLineSegment(sketch, "E70.3", {"start": v(-183.9, 7.62) * mm, "end": v(-183.9, 11.2) * mm});
            skLineSegment(sketch, "E70.4", {"start": v(-183.9, 11.2) * mm, "end": v(-180.8, 13) * mm});
            skLineSegment(sketch, "E70.5", {"start": v(-180.8, 13) * mm, "end": v(-177.7, 11.2) * mm});
            skCircle(sketch, "E71.cCircle", {"center": v(-173.78, 9.13) * mm, "radius": 2.92 * mm, "construction": true});
            skLineSegment(sketch, "E71.0", {"start": v(-170.86, 10.81) * mm, "end": v(-170.86, 7.44) * mm});
            skLineSegment(sketch, "E71.1", {"start": v(-170.86, 7.44) * mm, "end": v(-173.78, 5.76) * mm});
            skLineSegment(sketch, "E71.2", {"start": v(-173.78, 5.76) * mm, "end": v(-176.7, 7.44) * mm});
            skLineSegment(sketch, "E71.3", {"start": v(-176.7, 7.44) * mm, "end": v(-176.7, 10.81) * mm});
            skLineSegment(sketch, "E71.4", {"start": v(-176.7, 10.81) * mm, "end": v(-173.78, 12.5) * mm});
            skLineSegment(sketch, "E71.5", {"start": v(-173.78, 12.5) * mm, "end": v(-170.86, 10.81) * mm});
            skCircle(sketch, "E72.cCircle", {"center": v(-152.33, 8.55) * mm, "radius": 3.1 * mm, "construction": true});
            skLineSegment(sketch, "E72.0", {"start": v(-149.22, 10.34) * mm, "end": v(-149.22, 6.76) * mm});
            skLineSegment(sketch, "E72.1", {"start": v(-149.22, 6.76) * mm, "end": v(-152.33, 4.96) * mm});
            skLineSegment(sketch, "E72.2", {"start": v(-152.33, 4.96) * mm, "end": v(-155.43, 6.76) * mm});
            skLineSegment(sketch, "E72.3", {"start": v(-155.43, 6.76) * mm, "end": v(-155.43, 10.34) * mm});
            skLineSegment(sketch, "E72.4", {"start": v(-155.43, 10.34) * mm, "end": v(-152.33, 12.14) * mm});
            skLineSegment(sketch, "E72.5", {"start": v(-152.33, 12.14) * mm, "end": v(-149.22, 10.34) * mm});
            skCircle(sketch, "E73.cCircle", {"center": v(-166.75, 9.05) * mm, "radius": 3.1 * mm, "construction": true});
            skLineSegment(sketch, "E73.0", {"start": v(-163.65, 10.85) * mm, "end": v(-163.65, 7.26) * mm});
            skLineSegment(sketch, "E73.1", {"start": v(-163.65, 7.26) * mm, "end": v(-166.75, 5.47) * mm});
            skLineSegment(sketch, "E73.2", {"start": v(-166.75, 5.47) * mm, "end": v(-169.86, 7.26) * mm});
            skLineSegment(sketch, "E73.3", {"start": v(-169.86, 7.26) * mm, "end": v(-169.86, 10.85) * mm});
            skLineSegment(sketch, "E73.4", {"start": v(-169.86, 10.85) * mm, "end": v(-166.75, 12.64) * mm});
            skLineSegment(sketch, "E73.5", {"start": v(-166.75, 12.64) * mm, "end": v(-163.65, 10.85) * mm});
            skCircle(sketch, "E74.cCircle", {"center": v(-159.54, 8.9) * mm, "radius": 3.1 * mm, "construction": true});
            skLineSegment(sketch, "E74.0", {"start": v(-156.43, 10.69) * mm, "end": v(-156.43, 7.1) * mm});
            skLineSegment(sketch, "E74.1", {"start": v(-156.43, 7.1) * mm, "end": v(-159.54, 5.3) * mm});
            skLineSegment(sketch, "E74.2", {"start": v(-159.54, 5.3) * mm, "end": v(-162.65, 7.1) * mm});
            skLineSegment(sketch, "E74.3", {"start": v(-162.65, 7.1) * mm, "end": v(-162.65, 10.69) * mm});
            skLineSegment(sketch, "E74.4", {"start": v(-162.65, 10.69) * mm, "end": v(-159.54, 12.48) * mm});
            skLineSegment(sketch, "E74.5", {"start": v(-159.54, 12.48) * mm, "end": v(-156.43, 10.69) * mm});
            skArc(sketch, "E75", {"start": v(-367.34, 31.6) * mm, "mid": v(-318.4, -17.3) * mm, "end": v(-250.6, -31.12) * mm});
            skLineSegment(sketch, "E76", {"start": v(-250.6, -31.12) * mm, "end": v(-127.88, -26.55) * mm});
            skLineSegment(sketch, "E77", {"start": v(67.87, 7.77) * mm, "end": v(67.87, -7.84) * mm});
            skArc(sketch, "E78", {"start": v(67.87, 16.75) * mm, "mid": v(75.8, 7.15) * mm, "end": v(86, 0) * mm});
            skArc(sketch, "E79.MirrorCS", {"start": v(67.87, -16.75) * mm, "mid": v(75.8, -7.15) * mm, "end": v(86, 0) * mm});
            skArc(sketch, "E80", {"start": v(67.87, 7.77) * mm, "mid": v(71.51, 3.45) * mm, "end": v(75.98, 0) * mm});
            skArc(sketch, "E81.MirrorCS", {"start": v(67.87, -7.77) * mm, "mid": v(71.51, -3.45) * mm, "end": v(75.98, 0) * mm});
            skText(sketch, "E82", { "text": "bushido", "fontName": "OpenSans-Regular.ttf"});
            skCircle(sketch, "E83", {"center": v(-40, 0) * mm, "radius": 3.5 * mm});
            skCircle(sketch, "E84", {"center": v(40, 0) * mm, "radius": 3.5 * mm});
            const initialGuessF0  = {"E82": [0.06587, -0.01555, 0, 1, 0.00588]};
            skSetInitialGuess(sketch, initialGuessF0);
            skSolve(sketch);
        }
        {
            var Q0;
            Q0=makeQuery(id+"F0.imprint","IMPRINT",FACE,{"disambiguationData":[TD([[makeQuery(id+"F0.imprint","IMPRINT",EDGE,{"derivedFrom":sQuery(id+"F0.wireOp",EDGE,"E0")}),-1.0]])]});
            var Q1;
            {var subQ40=sQuery(id+"F0.wireOp",EDGE,"E30.1");Q1=makeQuery(id+"F0.imprint","IMPRINT",FACE,{"disambiguationData":[TD([[makeQuery(id+"F0.imprint","IMPRINT",EDGE,{"derivedFrom":subQ40}),1.0]])]});}
            var Q2;
            {var subQ0=sQuery(id+"F0.wireOp",EDGE,"E74.0");Q2=makeQuery(id+"F0.imprint","IMPRINT",FACE,{"disambiguationData":[TD([[makeQuery(id+"F0.imprint","IMPRINT",EDGE,{"derivedFrom":subQ0}),-1.0]])]});}
            var Q3;
            {var subQ0=sQuery(id+"F0.wireOp",EDGE,"E72.0");Q3=makeQuery(id+"F0.imprint","IMPRINT",FACE,{"disambiguationData":[TD([[makeQuery(id+"F0.imprint","IMPRINT",EDGE,{"derivedFrom":subQ0}),-1.0]])]});}
            var Q4;
            {var subQ1=sQuery(id+"F0.wireOp",EDGE,"E73.0");Q4=makeQuery(id+"F0.imprint","IMPRINT",FACE,{"disambiguationData":[TD([[makeQuery(id+"F0.imprint","IMPRINT",EDGE,{"derivedFrom":subQ1}),-1.0]])]});}
            var Q5;
            {var subQ0=sQuery(id+"F0.wireOp",EDGE,"E71.1");Q5=makeQuery(id+"F0.imprint","IMPRINT",FACE,{"disambiguationData":[TD([[makeQuery(id+"F0.imprint","IMPRINT",EDGE,{"derivedFrom":subQ0}),-1.0]])]});}
            var Q6;
            {var subQ0=sQuery(id+"F0.wireOp",EDGE,"E70.1");Q6=makeQuery(id+"F0.imprint","IMPRINT",FACE,{"disambiguationData":[TD([[makeQuery(id+"F0.imprint","IMPRINT",EDGE,{"derivedFrom":subQ0}),-1.0]])]});}
            var Q7;
            {var subQ0=sQuery(id+"F0.wireOp",EDGE,"E69.1");Q7=makeQuery(id+"F0.imprint","IMPRINT",FACE,{"disambiguationData":[TD([[makeQuery(id+"F0.imprint","IMPRINT",EDGE,{"derivedFrom":subQ0}),-1.0]])]});}
            var Q8;
            {var subQ0=sQuery(id+"F0.wireOp",EDGE,"E68.1");Q8=makeQuery(id+"F0.imprint","IMPRINT",FACE,{"disambiguationData":[TD([[makeQuery(id+"F0.imprint","IMPRINT",EDGE,{"derivedFrom":subQ0}),-1.0]])]});}
            var Q9;
            {var subQ0=sQuery(id+"F0.wireOp",EDGE,"E67.1");Q9=makeQuery(id+"F0.imprint","IMPRINT",FACE,{"disambiguationData":[TD([[makeQuery(id+"F0.imprint","IMPRINT",EDGE,{"derivedFrom":subQ0}),-1.0]])]});}
            var Q10;
            {var subQ0=sQuery(id+"F0.wireOp",EDGE,"E66.1");Q10=makeQuery(id+"F0.imprint","IMPRINT",FACE,{"disambiguationData":[TD([[makeQuery(id+"F0.imprint","IMPRINT",EDGE,{"derivedFrom":subQ0}),-1.0]])]});}
            var Q11;
            {var subQ0=sQuery(id+"F0.wireOp",EDGE,"E65.2");Q11=makeQuery(id+"F0.imprint","IMPRINT",FACE,{"disambiguationData":[TD([[makeQuery(id+"F0.imprint","IMPRINT",EDGE,{"derivedFrom":subQ0}),-1.0]])]});}
            var Q12;
            {var subQ5=sQuery(id+"F0.wireOp",EDGE,"E64.2");Q12=makeQuery(id+"F0.imprint","IMPRINT",FACE,{"disambiguationData":[TD([[makeQuery(id+"F0.imprint","IMPRINT",EDGE,{"derivedFrom":subQ5}),-1.0]])]});}
            var Q13;
            {var subQ1=sQuery(id+"F0.wireOp",EDGE,"E63.1");Q13=makeQuery(id+"F0.imprint","IMPRINT",FACE,{"disambiguationData":[TD([[makeQuery(id+"F0.imprint","IMPRINT",EDGE,{"derivedFrom":subQ1}),-1.0]])]});}
            var Q14;
            {var subQ1=sQuery(id+"F0.wireOp",EDGE,"E62.1");Q14=makeQuery(id+"F0.imprint","IMPRINT",FACE,{"disambiguationData":[TD([[makeQuery(id+"F0.imprint","IMPRINT",EDGE,{"derivedFrom":subQ1}),-1.0]])]});}
            var Q15;
            {var subQ0=sQuery(id+"F0.wireOp",EDGE,"E50.3");var subQ1=sQuery(id+"F0.wireOp",EDGE,"E28");var subQ2=makeQuery(id+"F0.imprint","INTERSECT",VERTEX,{"derivedFrom":[subQ1,subQ0]});Q15=makeQuery(id+"F0.imprint","IMPRINT",FACE,{"disambiguationData":[TD([[makeQuery(id+"F0.imprint","IMPRINT",EDGE,{"disambiguationData":[TD([[subQ2,-1.0]])],"derivedFrom":subQ1}),-1.0]])]});}
            var Q16;
            {var subQ0=sQuery(id+"F0.wireOp",EDGE,"E46.4");Q16=makeQuery(id+"F0.imprint","IMPRINT",FACE,{"disambiguationData":[TD([[makeQuery(id+"F0.imprint","IMPRINT",EDGE,{"derivedFrom":subQ0}),-1.0]])]});}
            var Q17;
            {var subQ0=sQuery(id+"F0.wireOp",EDGE,"E45.4");Q17=makeQuery(id+"F0.imprint","IMPRINT",FACE,{"disambiguationData":[TD([[makeQuery(id+"F0.imprint","IMPRINT",EDGE,{"derivedFrom":subQ0}),-1.0]])]});}
            var Q18;
            {var subQ0=sQuery(id+"F0.wireOp",EDGE,"E44.4");Q18=makeQuery(id+"F0.imprint","IMPRINT",FACE,{"disambiguationData":[TD([[makeQuery(id+"F0.imprint","IMPRINT",EDGE,{"derivedFrom":subQ0}),-1.0]])]});}
            var Q19;
            {var subQ0=sQuery(id+"F0.wireOp",EDGE,"E43.4");Q19=makeQuery(id+"F0.imprint","IMPRINT",FACE,{"disambiguationData":[TD([[makeQuery(id+"F0.imprint","IMPRINT",EDGE,{"derivedFrom":subQ0}),-1.0]])]});}
            var Q20;
            {var subQ0=sQuery(id+"F0.wireOp",EDGE,"E42.4");Q20=makeQuery(id+"F0.imprint","IMPRINT",FACE,{"disambiguationData":[TD([[makeQuery(id+"F0.imprint","IMPRINT",EDGE,{"derivedFrom":subQ0}),-1.0]])]});}
            var Q21;
            {var subQ0=sQuery(id+"F0.wireOp",EDGE,"E39.4");Q21=makeQuery(id+"F0.imprint","IMPRINT",FACE,{"disambiguationData":[TD([[makeQuery(id+"F0.imprint","IMPRINT",EDGE,{"derivedFrom":subQ0}),-1.0]])]});}
            var Q22;
            {var subQ0=sQuery(id+"F0.wireOp",EDGE,"E41.4");Q22=makeQuery(id+"F0.imprint","IMPRINT",FACE,{"disambiguationData":[TD([[makeQuery(id+"F0.imprint","IMPRINT",EDGE,{"derivedFrom":subQ0}),-1.0]])]});}
            var Q23;
            {var subQ0=sQuery(id+"F0.wireOp",EDGE,"E38.4");Q23=makeQuery(id+"F0.imprint","IMPRINT",FACE,{"disambiguationData":[TD([[makeQuery(id+"F0.imprint","IMPRINT",EDGE,{"derivedFrom":subQ0}),-1.0]])]});}
            var Q24;
            {var subQ0=sQuery(id+"F0.wireOp",EDGE,"E37.4");Q24=makeQuery(id+"F0.imprint","IMPRINT",FACE,{"disambiguationData":[TD([[makeQuery(id+"F0.imprint","IMPRINT",EDGE,{"derivedFrom":subQ0}),-1.0]])]});}
            var Q25;
            {var subQ0=sQuery(id+"F0.wireOp",EDGE,"E36.4");Q25=makeQuery(id+"F0.imprint","IMPRINT",FACE,{"disambiguationData":[TD([[makeQuery(id+"F0.imprint","IMPRINT",EDGE,{"derivedFrom":subQ0}),-1.0]])]});}
            var Q26;
            {var subQ0=sQuery(id+"F0.wireOp",EDGE,"E35.3");var subQ1=sQuery(id+"F0.wireOp",EDGE,"E26");var subQ2=makeQuery(id+"F0.imprint","INTERSECT",VERTEX,{"derivedFrom":[subQ1,subQ0]});Q26=makeQuery(id+"F0.imprint","IMPRINT",FACE,{"disambiguationData":[TD([[makeQuery(id+"F0.imprint","IMPRINT",EDGE,{"disambiguationData":[TD([[subQ2,-1.0]])],"derivedFrom":subQ1}),1.0]])]});}
            var Q27;
            {var subQ0=sQuery(id+"F0.wireOp",EDGE,"E34.4");var subQ1=sQuery(id+"F0.wireOp",EDGE,"E26");var subQ2=makeQuery(id+"F0.imprint","INTERSECT",VERTEX,{"derivedFrom":[subQ1,subQ0]});Q27=makeQuery(id+"F0.imprint","IMPRINT",FACE,{"disambiguationData":[TD([[makeQuery(id+"F0.imprint","IMPRINT",EDGE,{"disambiguationData":[TD([[subQ2,-1.0]])],"derivedFrom":subQ1}),1.0]])]});}
            var Q28;
            {var subQ0=sQuery(id+"F0.wireOp",EDGE,"E33.4");var subQ1=sQuery(id+"F0.wireOp",EDGE,"E26");var subQ2=makeQuery(id+"F0.imprint","INTERSECT",VERTEX,{"derivedFrom":[subQ1,subQ0]});Q28=makeQuery(id+"F0.imprint","IMPRINT",FACE,{"disambiguationData":[TD([[makeQuery(id+"F0.imprint","IMPRINT",EDGE,{"disambiguationData":[TD([[subQ2,-1.0]])],"derivedFrom":subQ1}),1.0]])]});}
            var Q29;
            {var subQ0=sQuery(id+"F0.wireOp",EDGE,"E30.3");var subQ1=sQuery(id+"F0.wireOp",EDGE,"E26");var subQ2=makeQuery(id+"F0.imprint","INTERSECT",VERTEX,{"derivedFrom":[subQ1,subQ0]});Q29=makeQuery(id+"F0.imprint","IMPRINT",FACE,{"disambiguationData":[TD([[makeQuery(id+"F0.imprint","IMPRINT",EDGE,{"disambiguationData":[TD([[subQ2,-1.0]])],"derivedFrom":subQ1}),1.0]])]});}
            var Q30;
            {var subQ0=sQuery(id+"F0.wireOp",EDGE,"E31.4");var subQ1=sQuery(id+"F0.wireOp",EDGE,"E26");var subQ2=makeQuery(id+"F0.imprint","INTERSECT",VERTEX,{"derivedFrom":[subQ1,subQ0]});Q30=makeQuery(id+"F0.imprint","IMPRINT",FACE,{"disambiguationData":[TD([[makeQuery(id+"F0.imprint","IMPRINT",EDGE,{"disambiguationData":[TD([[subQ2,-1.0]])],"derivedFrom":subQ1}),1.0]])]});}
            var Q31;
            {var subQ0=sQuery(id+"F0.wireOp",EDGE,"E32.4");var subQ1=sQuery(id+"F0.wireOp",EDGE,"E26");var subQ2=makeQuery(id+"F0.imprint","INTERSECT",VERTEX,{"derivedFrom":[subQ1,subQ0]});Q31=makeQuery(id+"F0.imprint","IMPRINT",FACE,{"disambiguationData":[TD([[makeQuery(id+"F0.imprint","IMPRINT",EDGE,{"disambiguationData":[TD([[subQ2,-1.0]])],"derivedFrom":subQ1}),1.0]])]});}
            var Q32;
            {var subQ0=sQuery(id+"F0.wireOp",EDGE,"E30.5");var subQ1=sQuery(id+"F0.wireOp",EDGE,"E27");var subQ2=makeQuery(id+"F0.imprint","INTERSECT",VERTEX,{"derivedFrom":[subQ1,subQ0]});Q32=makeQuery(id+"F0.imprint","IMPRINT",FACE,{"disambiguationData":[TD([[makeQuery(id+"F0.imprint","IMPRINT",EDGE,{"disambiguationData":[TD([[subQ2,-1.0]])],"derivedFrom":subQ1}),1.0]])]});}
            extrude(context, id + "F1", {"entities" : qUnion([Q0, Q1, Q2, Q3, Q4, Q5, Q6, Q7, Q8, Q9, Q10, Q11, Q12, Q13, Q14, Q15, Q16, Q17, Q18, Q19, Q20, Q21, Q22, Q23, Q24, Q25, Q26, Q27, Q28, Q29, Q30, Q31, Q32]), "depth" : 4 * mm});
        }
        {
            var Q0;
            Q0=qCreatedBy(makeId("Right.planeOp"),FACE);
            var sketch = newSketch(context, id + "F2", { "sketchPlane" : qUnion([Q0])});
            skLineSegment(sketch, "E85", {"start": v(0, 4.5) * mm, "end": v(-53.7, 0) * mm});
            skLineSegment(sketch, "E86", {"start": v(0, -0.7) * mm, "end": v(-53.7, 3.8) * mm});
            skLineSegment(sketch, "E87", {"start": v(0, 4.5) * mm, "end": v(-53.7, 3.8) * mm});
            skLineSegment(sketch, "E88", {"start": v(-53.7, 3.8) * mm, "end": v(-53.7, 0) * mm});
            skLineSegment(sketch, "E89", {"start": v(0, -0.7) * mm, "end": v(-53.7, 0) * mm});
            skSolve(sketch);
        }
        {
            var Q0;
            Q0 = qSketchRegion(id + "F2", true);
            extrude(context, id + "F3", {"entities" : qUnion([Q0]), "operationType" : NewBodyOperationType.REMOVE, "oppositeDirection" : true, "depth" : 429.6 * mm, "hasSecondDirection" : true, "secondDirectionOppositeDirection" : true, "secondDirectionDepth" : 133 * mm});
        }
        {
            var Q0;
            Q0=qCreatedBy(makeId("Front.planeOp"),FACE);
            var sketch = newSketch(context, id + "F4", { "sketchPlane" : qUnion([Q0])});
            skLineSegment(sketch, "E90", {"start": v(0, -8) * mm, "end": v(-370.72, 2) * mm});
            skLineSegment(sketch, "E91", {"start": v(0, 12) * mm, "end": v(-370.72, 2) * mm});
            skLineSegment(sketch, "E92", {"start": v(-370.72, 7.25) * mm, "end": v(-370.72, -3.05) * mm});
            skLineSegment(sketch, "E93", {"start": v(0, -8) * mm, "end": v(-370.72, -3.05) * mm});
            skLineSegment(sketch, "E94", {"start": v(0, 12) * mm, "end": v(-370.72, 7.25) * mm});
            skSolve(sketch);
        }
        {
            var Q0;
            Q0 = qSketchRegion(id + "F4", true);
            extrude(context, id + "F5", {"entities" : qUnion([Q0]), "operationType" : NewBodyOperationType.REMOVE, "endBound" : BoundingType.SYMMETRIC, "oppositeDirection" : true, "depth" : 105.6 * mm, "hasDraft" : true, "draftAngle" : 3 * degree});
        }
        {
            var Q0;
            Q0=makeQuery(id+"F1.opExtrude","CAP_FACE",FACE,{"disambiguationData":[OSD([sQuery(id+"F0.wireOp",EDGE,"E0"),sQuery(id+"F0.wireOp",EDGE,"ZRTyc1NL-TBSC-oep7-uRT5-nHEzeDgNGmcp"),sQuery(id+"F0.wireOp",EDGE,"E1"),sQuery(id+"F0.wireOp",EDGE,"E2"),sQuery(id+"F0.wireOp",EDGE,"E3"),sQuery(id+"F0.wireOp",EDGE,"E4"),sQuery(id+"F0.wireOp",EDGE,"E5"),sQuery(id+"F0.wireOp",EDGE,"fb6ad949-667d-40c5-bb62-eb53c9f7254e0.MirrorCS"),sQuery(id+"F0.wireOp",EDGE,"E6.MirrorCS"),sQuery(id+"F0.wireOp",EDGE,"E7.MirrorCS"),sQuery(id+"F0.wireOp",EDGE,"E8.MirrorCS"),sQuery(id+"F0.wireOp",EDGE,"E9.MirrorCS"),sQuery(id+"F0.wireOp",EDGE,"E10.MirrorCS"),sQuery(id+"F0.wireOp",EDGE,"E13.filletArc"),sQuery(id+"F0.wireOp",EDGE,"E14.filletArc"),sQuery(id+"F0.wireOp",EDGE,"E15"),sQuery(id+"F0.wireOp",EDGE,"E16"),sQuery(id+"F0.wireOp",EDGE,"9UYhI2y4-quXQ-nJSS-EsHa-6FkJM3KrFiao"),sQuery(id+"F0.wireOp",EDGE,"E18.filletArc"),sQuery(id+"F0.wireOp",EDGE,"E19"),sQuery(id+"F0.wireOp",EDGE,"E20"),sQuery(id+"F0.wireOp",EDGE,"E21"),sQuery(id+"F0.wireOp",EDGE,"E22"),sQuery(id+"F0.wireOp",EDGE,"E23"),sQuery(id+"F0.wireOp",EDGE,"E24"),sQuery(id+"F0.wireOp",EDGE,"E25"),sQuery(id+"F0.wireOp",EDGE,"E26"),sQuery(id+"F0.wireOp",EDGE,"E27"),sQuery(id+"F0.wireOp",EDGE,"E28"),sQuery(id+"F0.wireOp",EDGE,"6eYH2E0s-Vyh9-Uwo9-FMi5-A8Q6t3zVsnGa"),sQuery(id+"F0.wireOp",EDGE,"E29"),sQuery(id+"F0.wireOp",EDGE,"E30.0"),sQuery(id+"F0.wireOp",EDGE,"E30.1"),sQuery(id+"F0.wireOp",EDGE,"E30.2"),sQuery(id+"F0.wireOp",EDGE,"E30.3"),sQuery(id+"F0.wireOp",EDGE,"E31.0"),sQuery(id+"F0.wireOp",EDGE,"E31.1"),sQuery(id+"F0.wireOp",EDGE,"E31.2"),sQuery(id+"F0.wireOp",EDGE,"E31.3"),sQuery(id+"F0.wireOp",EDGE,"E31.4"),sQuery(id+"F0.wireOp",EDGE,"E31.5"),sQuery(id+"F0.wireOp",EDGE,"E32.0"),sQuery(id+"F0.wireOp",EDGE,"E32.1"),sQuery(id+"F0.wireOp",EDGE,"E32.2"),sQuery(id+"F0.wireOp",EDGE,"E32.3"),sQuery(id+"F0.wireOp",EDGE,"E32.4"),sQuery(id+"F0.wireOp",EDGE,"E32.5"),sQuery(id+"F0.wireOp",EDGE,"E33.0"),sQuery(id+"F0.wireOp",EDGE,"E33.1"),sQuery(id+"F0.wireOp",EDGE,"E33.2"),sQuery(id+"F0.wireOp",EDGE,"E33.3"),sQuery(id+"F0.wireOp",EDGE,"E33.4"),sQuery(id+"F0.wireOp",EDGE,"E33.5"),sQuery(id+"F0.wireOp",EDGE,"E34.0"),sQuery(id+"F0.wireOp",EDGE,"E34.1"),sQuery(id+"F0.wireOp",EDGE,"E34.2"),sQuery(id+"F0.wireOp",EDGE,"E34.3"),sQuery(id+"F0.wireOp",EDGE,"E34.4"),sQuery(id+"F0.wireOp",EDGE,"E34.5"),sQuery(id+"F0.wireOp",EDGE,"E35.0"),sQuery(id+"F0.wireOp",EDGE,"E35.1"),sQuery(id+"F0.wireOp",EDGE,"E35.2"),sQuery(id+"F0.wireOp",EDGE,"E35.3"),sQuery(id+"F0.wireOp",EDGE,"E35.4"),sQuery(id+"F0.wireOp",EDGE,"E35.5"),sQuery(id+"F0.wireOp",EDGE,"E36.0"),sQuery(id+"F0.wireOp",EDGE,"E36.1"),sQuery(id+"F0.wireOp",EDGE,"E36.2"),sQuery(id+"F0.wireOp",EDGE,"E36.3"),sQuery(id+"F0.wireOp",EDGE,"E37.0"),sQuery(id+"F0.wireOp",EDGE,"E37.1"),sQuery(id+"F0.wireOp",EDGE,"E37.2"),sQuery(id+"F0.wireOp",EDGE,"E37.3"),sQuery(id+"F0.wireOp",EDGE,"E38.0"),sQuery(id+"F0.wireOp",EDGE,"E38.1"),sQuery(id+"F0.wireOp",EDGE,"E38.2"),sQuery(id+"F0.wireOp",EDGE,"E38.3"),sQuery(id+"F0.wireOp",EDGE,"E39.0"),sQuery(id+"F0.wireOp",EDGE,"E39.1"),sQuery(id+"F0.wireOp",EDGE,"E39.2"),sQuery(id+"F0.wireOp",EDGE,"E39.3"),sQuery(id+"F0.wireOp",EDGE,"E41.0"),sQuery(id+"F0.wireOp",EDGE,"E41.1"),sQuery(id+"F0.wireOp",EDGE,"E41.2"),sQuery(id+"F0.wireOp",EDGE,"E41.3"),sQuery(id+"F0.wireOp",EDGE,"E42.0"),sQuery(id+"F0.wireOp",EDGE,"E42.1"),sQuery(id+"F0.wireOp",EDGE,"E42.2"),sQuery(id+"F0.wireOp",EDGE,"E42.3"),sQuery(id+"F0.wireOp",EDGE,"E43.0"),sQuery(id+"F0.wireOp",EDGE,"E43.1"),sQuery(id+"F0.wireOp",EDGE,"E43.2"),sQuery(id+"F0.wireOp",EDGE,"E43.3"),sQuery(id+"F0.wireOp",EDGE,"E44.0"),sQuery(id+"F0.wireOp",EDGE,"E44.1"),sQuery(id+"F0.wireOp",EDGE,"E44.2"),sQuery(id+"F0.wireOp",EDGE,"E44.3"),sQuery(id+"F0.wireOp",EDGE,"E45.0"),sQuery(id+"F0.wireOp",EDGE,"E45.1"),sQuery(id+"F0.wireOp",EDGE,"E45.2"),sQuery(id+"F0.wireOp",EDGE,"E45.3"),sQuery(id+"F0.wireOp",EDGE,"E46.0"),sQuery(id+"F0.wireOp",EDGE,"E46.1"),sQuery(id+"F0.wireOp",EDGE,"E46.2"),sQuery(id+"F0.wireOp",EDGE,"E46.3"),sQuery(id+"F0.wireOp",EDGE,"E47.0"),sQuery(id+"F0.wireOp",EDGE,"E47.1"),sQuery(id+"F0.wireOp",EDGE,"E47.2"),sQuery(id+"F0.wireOp",EDGE,"E47.3"),sQuery(id+"F0.wireOp",EDGE,"E47.4"),sQuery(id+"F0.wireOp",EDGE,"E47.5"),sQuery(id+"F0.wireOp",EDGE,"E48.0"),sQuery(id+"F0.wireOp",EDGE,"E48.1"),sQuery(id+"F0.wireOp",EDGE,"E48.2"),sQuery(id+"F0.wireOp",EDGE,"E48.3"),sQuery(id+"F0.wireOp",EDGE,"E48.4"),sQuery(id+"F0.wireOp",EDGE,"E48.5"),sQuery(id+"F0.wireOp",EDGE,"E49.0"),sQuery(id+"F0.wireOp",EDGE,"E49.1"),sQuery(id+"F0.wireOp",EDGE,"E49.2"),sQuery(id+"F0.wireOp",EDGE,"E49.3"),sQuery(id+"F0.wireOp",EDGE,"E49.4"),sQuery(id+"F0.wireOp",EDGE,"E49.5"),sQuery(id+"F0.wireOp",EDGE,"E50.0"),sQuery(id+"F0.wireOp",EDGE,"E50.1"),sQuery(id+"F0.wireOp",EDGE,"E50.3"),sQuery(id+"F0.wireOp",EDGE,"E50.4"),sQuery(id+"F0.wireOp",EDGE,"E50.5"),sQuery(id+"F0.wireOp",EDGE,"E51.0"),sQuery(id+"F0.wireOp",EDGE,"E51.1"),sQuery(id+"F0.wireOp",EDGE,"E51.2"),sQuery(id+"F0.wireOp",EDGE,"E51.3"),sQuery(id+"F0.wireOp",EDGE,"E51.4"),sQuery(id+"F0.wireOp",EDGE,"E51.5"),sQuery(id+"F0.wireOp",EDGE,"E52.0"),sQuery(id+"F0.wireOp",EDGE,"E52.1"),sQuery(id+"F0.wireOp",EDGE,"E52.2"),sQuery(id+"F0.wireOp",EDGE,"E52.3"),sQuery(id+"F0.wireOp",EDGE,"E52.4"),sQuery(id+"F0.wireOp",EDGE,"E52.5"),sQuery(id+"F0.wireOp",EDGE,"E53.0"),sQuery(id+"F0.wireOp",EDGE,"E53.1"),sQuery(id+"F0.wireOp",EDGE,"E53.2"),sQuery(id+"F0.wireOp",EDGE,"E53.3"),sQuery(id+"F0.wireOp",EDGE,"E53.4"),sQuery(id+"F0.wireOp",EDGE,"E53.5"),sQuery(id+"F0.wireOp",EDGE,"E54.0"),sQuery(id+"F0.wireOp",EDGE,"E54.1"),sQuery(id+"F0.wireOp",EDGE,"E54.2"),sQuery(id+"F0.wireOp",EDGE,"E54.3"),sQuery(id+"F0.wireOp",EDGE,"E54.4"),sQuery(id+"F0.wireOp",EDGE,"E54.5"),sQuery(id+"F0.wireOp",EDGE,"E55.0"),sQuery(id+"F0.wireOp",EDGE,"E55.1"),sQuery(id+"F0.wireOp",EDGE,"E55.2"),sQuery(id+"F0.wireOp",EDGE,"E55.3"),sQuery(id+"F0.wireOp",EDGE,"E55.4"),sQuery(id+"F0.wireOp",EDGE,"E55.5"),sQuery(id+"F0.wireOp",EDGE,"E56.0"),sQuery(id+"F0.wireOp",EDGE,"E56.1"),sQuery(id+"F0.wireOp",EDGE,"E56.2"),sQuery(id+"F0.wireOp",EDGE,"E56.3"),sQuery(id+"F0.wireOp",EDGE,"E56.4"),sQuery(id+"F0.wireOp",EDGE,"E56.5"),sQuery(id+"F0.wireOp",EDGE,"E57.0"),sQuery(id+"F0.wireOp",EDGE,"E57.1"),sQuery(id+"F0.wireOp",EDGE,"E57.2"),sQuery(id+"F0.wireOp",EDGE,"E57.3"),sQuery(id+"F0.wireOp",EDGE,"E57.4"),sQuery(id+"F0.wireOp",EDGE,"E57.5"),sQuery(id+"F0.wireOp",EDGE,"E58.0"),sQuery(id+"F0.wireOp",EDGE,"E58.1"),sQuery(id+"F0.wireOp",EDGE,"E58.2"),sQuery(id+"F0.wireOp",EDGE,"E58.3"),sQuery(id+"F0.wireOp",EDGE,"E58.4"),sQuery(id+"F0.wireOp",EDGE,"E58.5"),sQuery(id+"F0.wireOp",EDGE,"E59.0"),sQuery(id+"F0.wireOp",EDGE,"E59.1"),sQuery(id+"F0.wireOp",EDGE,"E59.2"),sQuery(id+"F0.wireOp",EDGE,"E59.3"),sQuery(id+"F0.wireOp",EDGE,"E59.4"),sQuery(id+"F0.wireOp",EDGE,"E59.5"),sQuery(id+"F0.wireOp",EDGE,"E60.0"),sQuery(id+"F0.wireOp",EDGE,"E60.1"),sQuery(id+"F0.wireOp",EDGE,"E60.2"),sQuery(id+"F0.wireOp",EDGE,"E60.3"),sQuery(id+"F0.wireOp",EDGE,"E60.4"),sQuery(id+"F0.wireOp",EDGE,"E60.5"),sQuery(id+"F0.wireOp",EDGE,"E61.0"),sQuery(id+"F0.wireOp",EDGE,"E61.1"),sQuery(id+"F0.wireOp",EDGE,"E61.2"),sQuery(id+"F0.wireOp",EDGE,"E61.3"),sQuery(id+"F0.wireOp",EDGE,"E61.4"),sQuery(id+"F0.wireOp",EDGE,"E61.5"),sQuery(id+"F0.wireOp",EDGE,"E62.0"),sQuery(id+"F0.wireOp",EDGE,"E62.3"),sQuery(id+"F0.wireOp",EDGE,"E62.4"),sQuery(id+"F0.wireOp",EDGE,"E62.5"),sQuery(id+"F0.wireOp",EDGE,"E63.0"),sQuery(id+"F0.wireOp",EDGE,"E63.3"),sQuery(id+"F0.wireOp",EDGE,"E63.4"),sQuery(id+"F0.wireOp",EDGE,"E63.5"),sQuery(id+"F0.wireOp",EDGE,"E64.0"),sQuery(id+"F0.wireOp",EDGE,"E64.1"),sQuery(id+"F0.wireOp",EDGE,"E64.3"),sQuery(id+"F0.wireOp",EDGE,"E64.4"),sQuery(id+"F0.wireOp",EDGE,"E64.5"),sQuery(id+"F0.wireOp",EDGE,"E65.0"),sQuery(id+"F0.wireOp",EDGE,"E65.1"),sQuery(id+"F0.wireOp",EDGE,"E65.3"),sQuery(id+"F0.wireOp",EDGE,"E65.4"),sQuery(id+"F0.wireOp",EDGE,"E65.5"),sQuery(id+"F0.wireOp",EDGE,"E66.0"),sQuery(id+"F0.wireOp",EDGE,"E66.3"),sQuery(id+"F0.wireOp",EDGE,"E66.4"),sQuery(id+"F0.wireOp",EDGE,"E66.5"),sQuery(id+"F0.wireOp",EDGE,"E67.0"),sQuery(id+"F0.wireOp",EDGE,"E67.3"),sQuery(id+"F0.wireOp",EDGE,"E67.4"),sQuery(id+"F0.wireOp",EDGE,"E67.5"),sQuery(id+"F0.wireOp",EDGE,"E68.0"),sQuery(id+"F0.wireOp",EDGE,"E68.3"),sQuery(id+"F0.wireOp",EDGE,"E68.4"),sQuery(id+"F0.wireOp",EDGE,"E68.5"),sQuery(id+"F0.wireOp",EDGE,"E69.0"),sQuery(id+"F0.wireOp",EDGE,"E69.3"),sQuery(id+"F0.wireOp",EDGE,"E69.4"),sQuery(id+"F0.wireOp",EDGE,"E69.5"),sQuery(id+"F0.wireOp",EDGE,"E70.0"),sQuery(id+"F0.wireOp",EDGE,"E70.3"),sQuery(id+"F0.wireOp",EDGE,"E70.4"),sQuery(id+"F0.wireOp",EDGE,"E70.5"),sQuery(id+"F0.wireOp",EDGE,"E71.0"),sQuery(id+"F0.wireOp",EDGE,"E71.3"),sQuery(id+"F0.wireOp",EDGE,"E71.4"),sQuery(id+"F0.wireOp",EDGE,"E71.5"),sQuery(id+"F0.wireOp",EDGE,"E72.4"),sQuery(id+"F0.wireOp",EDGE,"E72.5"),sQuery(id+"F0.wireOp",EDGE,"E73.3"),sQuery(id+"F0.wireOp",EDGE,"E73.4"),sQuery(id+"F0.wireOp",EDGE,"E73.5"),sQuery(id+"F0.wireOp",EDGE,"E74.4"),sQuery(id+"F0.wireOp",EDGE,"E74.5")])],"isStart":false});
            var sketch = newSketch(context, id + "F6", { "sketchPlane" : qUnion([Q0])});
            skArc(sketch, "E95", {"start": v(-107.9, 21.49) * mm, "mid": v(-123.57, 0) * mm, "end": v(-107.78, -21.4) * mm});
            skArc(sketch, "E96", {"start": v(-101.7, 24.98) * mm, "mid": v(-126.29, -0.06) * mm, "end": v(-101.7, -25.1) * mm});
            skArc(sketch, "E97", {"start": v(-101.7, 24.98) * mm, "mid": v(-105.11, 23.78) * mm, "end": v(-107.9, 21.49) * mm});
            skArc(sketch, "E98", {"start": v(-107.78, -21.4) * mm, "mid": v(-105.07, -23.78) * mm, "end": v(-101.7, -25.1) * mm});
            skLineSegment(sketch, "E99", {"start": v(-101.7, 42.91) * mm, "end": v(-101.7, -41.03) * mm, "construction": true});
            skArc(sketch, "E100", {"start": v(-108.36, 21.48) * mm, "mid": v(-123.8, -0.17) * mm, "end": v(-107.78, -21.4) * mm});
            skArc(sketch, "E101", {"start": v(-102.17, 24.97) * mm, "mid": v(-126.74, -0.29) * mm, "end": v(-101.7, -25.1) * mm});
            skArc(sketch, "E102", {"start": v(-102.17, 24.97) * mm, "mid": v(-105.57, 23.77) * mm, "end": v(-108.36, 21.48) * mm});
            skSolve(sketch);
        }
        {
            var Q0;
            Q0 = qSketchRegion(id + "F6", true);
            extrude(context, id + "F7", {"entities" : qUnion([Q0]), "depth" : 3 * mm});
        }
        {
            var Q0;
            Q0=makeQuery(id+"F1.opExtrude","CAP_FACE",FACE,{"disambiguationData":[OSD([sQuery(id+"F0.wireOp",EDGE,"E0"),sQuery(id+"F0.wireOp",EDGE,"ZRTyc1NL-TBSC-oep7-uRT5-nHEzeDgNGmcp"),sQuery(id+"F0.wireOp",EDGE,"E1"),sQuery(id+"F0.wireOp",EDGE,"E2"),sQuery(id+"F0.wireOp",EDGE,"E3"),sQuery(id+"F0.wireOp",EDGE,"E4"),sQuery(id+"F0.wireOp",EDGE,"E5"),sQuery(id+"F0.wireOp",EDGE,"fb6ad949-667d-40c5-bb62-eb53c9f7254e0.MirrorCS"),sQuery(id+"F0.wireOp",EDGE,"E6.MirrorCS"),sQuery(id+"F0.wireOp",EDGE,"E7.MirrorCS"),sQuery(id+"F0.wireOp",EDGE,"E8.MirrorCS"),sQuery(id+"F0.wireOp",EDGE,"E9.MirrorCS"),sQuery(id+"F0.wireOp",EDGE,"E10.MirrorCS"),sQuery(id+"F0.wireOp",EDGE,"E13.filletArc"),sQuery(id+"F0.wireOp",EDGE,"E14.filletArc"),sQuery(id+"F0.wireOp",EDGE,"E15"),sQuery(id+"F0.wireOp",EDGE,"E16"),sQuery(id+"F0.wireOp",EDGE,"E18.filletArc"),sQuery(id+"F0.wireOp",EDGE,"E19"),sQuery(id+"F0.wireOp",EDGE,"E20"),sQuery(id+"F0.wireOp",EDGE,"E21"),sQuery(id+"F0.wireOp",EDGE,"E22"),sQuery(id+"F0.wireOp",EDGE,"E23"),sQuery(id+"F0.wireOp",EDGE,"E24"),sQuery(id+"F0.wireOp",EDGE,"E25"),sQuery(id+"F0.wireOp",EDGE,"E26"),sQuery(id+"F0.wireOp",EDGE,"E27"),sQuery(id+"F0.wireOp",EDGE,"E28"),sQuery(id+"F0.wireOp",EDGE,"6eYH2E0s-Vyh9-Uwo9-FMi5-A8Q6t3zVsnGa"),sQuery(id+"F0.wireOp",EDGE,"E29"),sQuery(id+"F0.wireOp",EDGE,"E30.0"),sQuery(id+"F0.wireOp",EDGE,"E30.1"),sQuery(id+"F0.wireOp",EDGE,"E30.2"),sQuery(id+"F0.wireOp",EDGE,"E30.3"),sQuery(id+"F0.wireOp",EDGE,"E31.0"),sQuery(id+"F0.wireOp",EDGE,"E31.1"),sQuery(id+"F0.wireOp",EDGE,"E31.2"),sQuery(id+"F0.wireOp",EDGE,"E31.3"),sQuery(id+"F0.wireOp",EDGE,"E31.4"),sQuery(id+"F0.wireOp",EDGE,"E31.5"),sQuery(id+"F0.wireOp",EDGE,"E32.0"),sQuery(id+"F0.wireOp",EDGE,"E32.1"),sQuery(id+"F0.wireOp",EDGE,"E32.2"),sQuery(id+"F0.wireOp",EDGE,"E32.3"),sQuery(id+"F0.wireOp",EDGE,"E32.4"),sQuery(id+"F0.wireOp",EDGE,"E32.5"),sQuery(id+"F0.wireOp",EDGE,"E33.0"),sQuery(id+"F0.wireOp",EDGE,"E33.1"),sQuery(id+"F0.wireOp",EDGE,"E33.2"),sQuery(id+"F0.wireOp",EDGE,"E33.3"),sQuery(id+"F0.wireOp",EDGE,"E33.4"),sQuery(id+"F0.wireOp",EDGE,"E33.5"),sQuery(id+"F0.wireOp",EDGE,"E34.0"),sQuery(id+"F0.wireOp",EDGE,"E34.1"),sQuery(id+"F0.wireOp",EDGE,"E34.2"),sQuery(id+"F0.wireOp",EDGE,"E34.3"),sQuery(id+"F0.wireOp",EDGE,"E34.4"),sQuery(id+"F0.wireOp",EDGE,"E34.5"),sQuery(id+"F0.wireOp",EDGE,"E35.0"),sQuery(id+"F0.wireOp",EDGE,"E35.1"),sQuery(id+"F0.wireOp",EDGE,"E35.2"),sQuery(id+"F0.wireOp",EDGE,"E35.3"),sQuery(id+"F0.wireOp",EDGE,"E35.4"),sQuery(id+"F0.wireOp",EDGE,"E35.5"),sQuery(id+"F0.wireOp",EDGE,"E36.0"),sQuery(id+"F0.wireOp",EDGE,"E36.1"),sQuery(id+"F0.wireOp",EDGE,"E36.2"),sQuery(id+"F0.wireOp",EDGE,"E36.3"),sQuery(id+"F0.wireOp",EDGE,"E37.0"),sQuery(id+"F0.wireOp",EDGE,"E37.1"),sQuery(id+"F0.wireOp",EDGE,"E37.2"),sQuery(id+"F0.wireOp",EDGE,"E37.3"),sQuery(id+"F0.wireOp",EDGE,"E38.0"),sQuery(id+"F0.wireOp",EDGE,"E38.1"),sQuery(id+"F0.wireOp",EDGE,"E38.2"),sQuery(id+"F0.wireOp",EDGE,"E38.3"),sQuery(id+"F0.wireOp",EDGE,"E39.0"),sQuery(id+"F0.wireOp",EDGE,"E39.1"),sQuery(id+"F0.wireOp",EDGE,"E39.2"),sQuery(id+"F0.wireOp",EDGE,"E39.3"),sQuery(id+"F0.wireOp",EDGE,"E41.0"),sQuery(id+"F0.wireOp",EDGE,"E41.1"),sQuery(id+"F0.wireOp",EDGE,"E41.2"),sQuery(id+"F0.wireOp",EDGE,"E41.3"),sQuery(id+"F0.wireOp",EDGE,"E42.0"),sQuery(id+"F0.wireOp",EDGE,"E42.1"),sQuery(id+"F0.wireOp",EDGE,"E42.2"),sQuery(id+"F0.wireOp",EDGE,"E42.3"),sQuery(id+"F0.wireOp",EDGE,"E43.0"),sQuery(id+"F0.wireOp",EDGE,"E43.1"),sQuery(id+"F0.wireOp",EDGE,"E43.2"),sQuery(id+"F0.wireOp",EDGE,"E43.3"),sQuery(id+"F0.wireOp",EDGE,"E44.0"),sQuery(id+"F0.wireOp",EDGE,"E44.1"),sQuery(id+"F0.wireOp",EDGE,"E44.2"),sQuery(id+"F0.wireOp",EDGE,"E44.3"),sQuery(id+"F0.wireOp",EDGE,"E45.0"),sQuery(id+"F0.wireOp",EDGE,"E45.1"),sQuery(id+"F0.wireOp",EDGE,"E45.2"),sQuery(id+"F0.wireOp",EDGE,"E45.3"),sQuery(id+"F0.wireOp",EDGE,"E46.0"),sQuery(id+"F0.wireOp",EDGE,"E46.1"),sQuery(id+"F0.wireOp",EDGE,"E46.2"),sQuery(id+"F0.wireOp",EDGE,"E46.3"),sQuery(id+"F0.wireOp",EDGE,"E47.0"),sQuery(id+"F0.wireOp",EDGE,"E47.1"),sQuery(id+"F0.wireOp",EDGE,"E47.2"),sQuery(id+"F0.wireOp",EDGE,"E47.3"),sQuery(id+"F0.wireOp",EDGE,"E47.4"),sQuery(id+"F0.wireOp",EDGE,"E47.5"),sQuery(id+"F0.wireOp",EDGE,"E48.0"),sQuery(id+"F0.wireOp",EDGE,"E48.1"),sQuery(id+"F0.wireOp",EDGE,"E48.2"),sQuery(id+"F0.wireOp",EDGE,"E48.3"),sQuery(id+"F0.wireOp",EDGE,"E48.4"),sQuery(id+"F0.wireOp",EDGE,"E48.5"),sQuery(id+"F0.wireOp",EDGE,"E49.0"),sQuery(id+"F0.wireOp",EDGE,"E49.1"),sQuery(id+"F0.wireOp",EDGE,"E49.2"),sQuery(id+"F0.wireOp",EDGE,"E49.3"),sQuery(id+"F0.wireOp",EDGE,"E49.4"),sQuery(id+"F0.wireOp",EDGE,"E49.5"),sQuery(id+"F0.wireOp",EDGE,"E50.0"),sQuery(id+"F0.wireOp",EDGE,"E50.1"),sQuery(id+"F0.wireOp",EDGE,"E50.3"),sQuery(id+"F0.wireOp",EDGE,"E50.4"),sQuery(id+"F0.wireOp",EDGE,"E50.5"),sQuery(id+"F0.wireOp",EDGE,"E51.0"),sQuery(id+"F0.wireOp",EDGE,"E51.1"),sQuery(id+"F0.wireOp",EDGE,"E51.2"),sQuery(id+"F0.wireOp",EDGE,"E51.3"),sQuery(id+"F0.wireOp",EDGE,"E51.4"),sQuery(id+"F0.wireOp",EDGE,"E51.5"),sQuery(id+"F0.wireOp",EDGE,"E52.0"),sQuery(id+"F0.wireOp",EDGE,"E52.1"),sQuery(id+"F0.wireOp",EDGE,"E52.2"),sQuery(id+"F0.wireOp",EDGE,"E52.3"),sQuery(id+"F0.wireOp",EDGE,"E52.4"),sQuery(id+"F0.wireOp",EDGE,"E52.5"),sQuery(id+"F0.wireOp",EDGE,"E53.0"),sQuery(id+"F0.wireOp",EDGE,"E53.1"),sQuery(id+"F0.wireOp",EDGE,"E53.2"),sQuery(id+"F0.wireOp",EDGE,"E53.3"),sQuery(id+"F0.wireOp",EDGE,"E53.4"),sQuery(id+"F0.wireOp",EDGE,"E53.5"),sQuery(id+"F0.wireOp",EDGE,"E54.0"),sQuery(id+"F0.wireOp",EDGE,"E54.1"),sQuery(id+"F0.wireOp",EDGE,"E54.2"),sQuery(id+"F0.wireOp",EDGE,"E54.3"),sQuery(id+"F0.wireOp",EDGE,"E54.4"),sQuery(id+"F0.wireOp",EDGE,"E54.5"),sQuery(id+"F0.wireOp",EDGE,"E55.0"),sQuery(id+"F0.wireOp",EDGE,"E55.1"),sQuery(id+"F0.wireOp",EDGE,"E55.2"),sQuery(id+"F0.wireOp",EDGE,"E55.3"),sQuery(id+"F0.wireOp",EDGE,"E55.4"),sQuery(id+"F0.wireOp",EDGE,"E55.5"),sQuery(id+"F0.wireOp",EDGE,"E56.0"),sQuery(id+"F0.wireOp",EDGE,"E56.1"),sQuery(id+"F0.wireOp",EDGE,"E56.2"),sQuery(id+"F0.wireOp",EDGE,"E56.3"),sQuery(id+"F0.wireOp",EDGE,"E56.4"),sQuery(id+"F0.wireOp",EDGE,"E56.5"),sQuery(id+"F0.wireOp",EDGE,"E57.0"),sQuery(id+"F0.wireOp",EDGE,"E57.1"),sQuery(id+"F0.wireOp",EDGE,"E57.2"),sQuery(id+"F0.wireOp",EDGE,"E57.3"),sQuery(id+"F0.wireOp",EDGE,"E57.4"),sQuery(id+"F0.wireOp",EDGE,"E57.5"),sQuery(id+"F0.wireOp",EDGE,"E58.0"),sQuery(id+"F0.wireOp",EDGE,"E58.1"),sQuery(id+"F0.wireOp",EDGE,"E58.2"),sQuery(id+"F0.wireOp",EDGE,"E58.3"),sQuery(id+"F0.wireOp",EDGE,"E58.4"),sQuery(id+"F0.wireOp",EDGE,"E58.5"),sQuery(id+"F0.wireOp",EDGE,"E59.0"),sQuery(id+"F0.wireOp",EDGE,"E59.1"),sQuery(id+"F0.wireOp",EDGE,"E59.2"),sQuery(id+"F0.wireOp",EDGE,"E59.3"),sQuery(id+"F0.wireOp",EDGE,"E59.4"),sQuery(id+"F0.wireOp",EDGE,"E59.5"),sQuery(id+"F0.wireOp",EDGE,"E60.0"),sQuery(id+"F0.wireOp",EDGE,"E60.1"),sQuery(id+"F0.wireOp",EDGE,"E60.2"),sQuery(id+"F0.wireOp",EDGE,"E60.3"),sQuery(id+"F0.wireOp",EDGE,"E60.4"),sQuery(id+"F0.wireOp",EDGE,"E60.5"),sQuery(id+"F0.wireOp",EDGE,"E61.0"),sQuery(id+"F0.wireOp",EDGE,"E61.1"),sQuery(id+"F0.wireOp",EDGE,"E61.2"),sQuery(id+"F0.wireOp",EDGE,"E61.3"),sQuery(id+"F0.wireOp",EDGE,"E61.4"),sQuery(id+"F0.wireOp",EDGE,"E61.5"),sQuery(id+"F0.wireOp",EDGE,"E62.0"),sQuery(id+"F0.wireOp",EDGE,"E62.3"),sQuery(id+"F0.wireOp",EDGE,"E62.4"),sQuery(id+"F0.wireOp",EDGE,"E62.5"),sQuery(id+"F0.wireOp",EDGE,"E63.0"),sQuery(id+"F0.wireOp",EDGE,"E63.3"),sQuery(id+"F0.wireOp",EDGE,"E63.4"),sQuery(id+"F0.wireOp",EDGE,"E63.5"),sQuery(id+"F0.wireOp",EDGE,"E64.0"),sQuery(id+"F0.wireOp",EDGE,"E64.1"),sQuery(id+"F0.wireOp",EDGE,"E64.3"),sQuery(id+"F0.wireOp",EDGE,"E64.4"),sQuery(id+"F0.wireOp",EDGE,"E64.5"),sQuery(id+"F0.wireOp",EDGE,"E65.0"),sQuery(id+"F0.wireOp",EDGE,"E65.1"),sQuery(id+"F0.wireOp",EDGE,"E65.3"),sQuery(id+"F0.wireOp",EDGE,"E65.4"),sQuery(id+"F0.wireOp",EDGE,"E65.5"),sQuery(id+"F0.wireOp",EDGE,"E66.0"),sQuery(id+"F0.wireOp",EDGE,"E66.3"),sQuery(id+"F0.wireOp",EDGE,"E66.4"),sQuery(id+"F0.wireOp",EDGE,"E66.5"),sQuery(id+"F0.wireOp",EDGE,"E67.0"),sQuery(id+"F0.wireOp",EDGE,"E67.3"),sQuery(id+"F0.wireOp",EDGE,"E67.4"),sQuery(id+"F0.wireOp",EDGE,"E67.5"),sQuery(id+"F0.wireOp",EDGE,"E68.0"),sQuery(id+"F0.wireOp",EDGE,"E68.3"),sQuery(id+"F0.wireOp",EDGE,"E68.4"),sQuery(id+"F0.wireOp",EDGE,"E68.5"),sQuery(id+"F0.wireOp",EDGE,"E69.0"),sQuery(id+"F0.wireOp",EDGE,"E69.3"),sQuery(id+"F0.wireOp",EDGE,"E69.4"),sQuery(id+"F0.wireOp",EDGE,"E69.5"),sQuery(id+"F0.wireOp",EDGE,"E70.0"),sQuery(id+"F0.wireOp",EDGE,"E70.3"),sQuery(id+"F0.wireOp",EDGE,"E70.4"),sQuery(id+"F0.wireOp",EDGE,"E70.5"),sQuery(id+"F0.wireOp",EDGE,"E71.0"),sQuery(id+"F0.wireOp",EDGE,"E71.3"),sQuery(id+"F0.wireOp",EDGE,"E71.4"),sQuery(id+"F0.wireOp",EDGE,"E71.5"),sQuery(id+"F0.wireOp",EDGE,"E72.4"),sQuery(id+"F0.wireOp",EDGE,"E72.5"),sQuery(id+"F0.wireOp",EDGE,"E73.3"),sQuery(id+"F0.wireOp",EDGE,"E73.4"),sQuery(id+"F0.wireOp",EDGE,"E73.5"),sQuery(id+"F0.wireOp",EDGE,"E74.4"),sQuery(id+"F0.wireOp",EDGE,"E74.5"),sQuery(id+"F0.wireOp",EDGE,"E75")])],"isStart":true});
            var sketch = newSketch(context, id + "F8", { "sketchPlane" : qUnion([Q0])});
            skArc(sketch, "E103", {"start": v(-108.4, 21.67) * mm, "mid": v(-124.07, 0.18) * mm, "end": v(-108.27, -21.22) * mm});
            skArc(sketch, "E104", {"start": v(-102.2, 25.16) * mm, "mid": v(-126.79, 0.12) * mm, "end": v(-102.2, -24.91) * mm});
            skArc(sketch, "E105", {"start": v(-102.2, 25.16) * mm, "mid": v(-105.6, 23.96) * mm, "end": v(-108.4, 21.67) * mm});
            skArc(sketch, "E106", {"start": v(-108.27, -21.22) * mm, "mid": v(-105.57, -23.6) * mm, "end": v(-102.2, -24.91) * mm});
            skLineSegment(sketch, "E107", {"start": v(-102.2, 61.3) * mm, "end": v(-101.17, -59.4) * mm, "construction": true});
            skSolve(sketch);
        }
        {
            var Q0;
            Q0 = qSketchRegion(id + "F8", true);
            extrude(context, id + "F9", {"entities" : qUnion([Q0]), "depth" : 3 * mm});
        }
        {
            var Q0;
            Q0=makeQuery(id+"F9.opExtrude","CAP_EDGE",EDGE,{"disambiguationData":[OSD([sQuery(id+"F8.wireOp",EDGE,"E103")])],"isStart":false});
            var Q1;
            Q1=makeQuery(id+"F9.opExtrude","CAP_EDGE",EDGE,{"disambiguationData":[OSD([sQuery(id+"F8.wireOp",EDGE,"E104")])],"isStart":false});
            var Q2;
            Q2=makeQuery(id+"F7.opExtrude","CAP_EDGE",EDGE,{"disambiguationData":[OSD([sQuery(id+"F6.wireOp",EDGE,"E95")])],"isStart":false});
            var Q3;
            Q3=makeQuery(id+"F7.opExtrude","CAP_EDGE",EDGE,{"disambiguationData":[OSD([sQuery(id+"F6.wireOp",EDGE,"E101")])],"isStart":false});
            chamfer(context, id + "F10", {"entities" : qUnion([Q0, Q1, Q2, Q3]), "width" : 1 * mm, "tangentPropagation" : true});
        }
        {
            var Q0;
            Q0=makeQuery(id+"F1.opExtrude","CAP_FACE",FACE,{"disambiguationData":[OSD([sQuery(id+"F0.wireOp",EDGE,"E0"),sQuery(id+"F0.wireOp",EDGE,"ZRTyc1NL-TBSC-oep7-uRT5-nHEzeDgNGmcp"),sQuery(id+"F0.wireOp",EDGE,"E1"),sQuery(id+"F0.wireOp",EDGE,"E2"),sQuery(id+"F0.wireOp",EDGE,"E3"),sQuery(id+"F0.wireOp",EDGE,"E4"),sQuery(id+"F0.wireOp",EDGE,"E5"),sQuery(id+"F0.wireOp",EDGE,"fb6ad949-667d-40c5-bb62-eb53c9f7254e0.MirrorCS"),sQuery(id+"F0.wireOp",EDGE,"E6.MirrorCS"),sQuery(id+"F0.wireOp",EDGE,"E7.MirrorCS"),sQuery(id+"F0.wireOp",EDGE,"E8.MirrorCS"),sQuery(id+"F0.wireOp",EDGE,"E9.MirrorCS"),sQuery(id+"F0.wireOp",EDGE,"E10.MirrorCS"),sQuery(id+"F0.wireOp",EDGE,"E13.filletArc"),sQuery(id+"F0.wireOp",EDGE,"E14.filletArc"),sQuery(id+"F0.wireOp",EDGE,"E15"),sQuery(id+"F0.wireOp",EDGE,"E16"),sQuery(id+"F0.wireOp",EDGE,"E18.filletArc"),sQuery(id+"F0.wireOp",EDGE,"E19"),sQuery(id+"F0.wireOp",EDGE,"E20"),sQuery(id+"F0.wireOp",EDGE,"E21"),sQuery(id+"F0.wireOp",EDGE,"E22"),sQuery(id+"F0.wireOp",EDGE,"E23"),sQuery(id+"F0.wireOp",EDGE,"E24"),sQuery(id+"F0.wireOp",EDGE,"E25"),sQuery(id+"F0.wireOp",EDGE,"E26"),sQuery(id+"F0.wireOp",EDGE,"E27"),sQuery(id+"F0.wireOp",EDGE,"E28"),sQuery(id+"F0.wireOp",EDGE,"E29"),sQuery(id+"F0.wireOp",EDGE,"E30.0"),sQuery(id+"F0.wireOp",EDGE,"E30.1"),sQuery(id+"F0.wireOp",EDGE,"E30.2"),sQuery(id+"F0.wireOp",EDGE,"E30.3"),sQuery(id+"F0.wireOp",EDGE,"E31.0"),sQuery(id+"F0.wireOp",EDGE,"E31.1"),sQuery(id+"F0.wireOp",EDGE,"E31.2"),sQuery(id+"F0.wireOp",EDGE,"E31.3"),sQuery(id+"F0.wireOp",EDGE,"E31.4"),sQuery(id+"F0.wireOp",EDGE,"E31.5"),sQuery(id+"F0.wireOp",EDGE,"E32.0"),sQuery(id+"F0.wireOp",EDGE,"E32.1"),sQuery(id+"F0.wireOp",EDGE,"E32.2"),sQuery(id+"F0.wireOp",EDGE,"E32.3"),sQuery(id+"F0.wireOp",EDGE,"E32.4"),sQuery(id+"F0.wireOp",EDGE,"E32.5"),sQuery(id+"F0.wireOp",EDGE,"E33.0"),sQuery(id+"F0.wireOp",EDGE,"E33.1"),sQuery(id+"F0.wireOp",EDGE,"E33.2"),sQuery(id+"F0.wireOp",EDGE,"E33.3"),sQuery(id+"F0.wireOp",EDGE,"E33.4"),sQuery(id+"F0.wireOp",EDGE,"E33.5"),sQuery(id+"F0.wireOp",EDGE,"E34.0"),sQuery(id+"F0.wireOp",EDGE,"E34.1"),sQuery(id+"F0.wireOp",EDGE,"E34.2"),sQuery(id+"F0.wireOp",EDGE,"E34.3"),sQuery(id+"F0.wireOp",EDGE,"E34.4"),sQuery(id+"F0.wireOp",EDGE,"E34.5"),sQuery(id+"F0.wireOp",EDGE,"E35.0"),sQuery(id+"F0.wireOp",EDGE,"E35.1"),sQuery(id+"F0.wireOp",EDGE,"E35.2"),sQuery(id+"F0.wireOp",EDGE,"E35.3"),sQuery(id+"F0.wireOp",EDGE,"E35.4"),sQuery(id+"F0.wireOp",EDGE,"E35.5"),sQuery(id+"F0.wireOp",EDGE,"E36.0"),sQuery(id+"F0.wireOp",EDGE,"E36.1"),sQuery(id+"F0.wireOp",EDGE,"E36.2"),sQuery(id+"F0.wireOp",EDGE,"E36.3"),sQuery(id+"F0.wireOp",EDGE,"E37.0"),sQuery(id+"F0.wireOp",EDGE,"E37.1"),sQuery(id+"F0.wireOp",EDGE,"E37.2"),sQuery(id+"F0.wireOp",EDGE,"E37.3"),sQuery(id+"F0.wireOp",EDGE,"E38.0"),sQuery(id+"F0.wireOp",EDGE,"E38.1"),sQuery(id+"F0.wireOp",EDGE,"E38.2"),sQuery(id+"F0.wireOp",EDGE,"E38.3"),sQuery(id+"F0.wireOp",EDGE,"E39.0"),sQuery(id+"F0.wireOp",EDGE,"E39.1"),sQuery(id+"F0.wireOp",EDGE,"E39.2"),sQuery(id+"F0.wireOp",EDGE,"E39.3"),sQuery(id+"F0.wireOp",EDGE,"E41.0"),sQuery(id+"F0.wireOp",EDGE,"E41.1"),sQuery(id+"F0.wireOp",EDGE,"E41.2"),sQuery(id+"F0.wireOp",EDGE,"E41.3"),sQuery(id+"F0.wireOp",EDGE,"E42.0"),sQuery(id+"F0.wireOp",EDGE,"E42.1"),sQuery(id+"F0.wireOp",EDGE,"E42.2"),sQuery(id+"F0.wireOp",EDGE,"E42.3"),sQuery(id+"F0.wireOp",EDGE,"E43.0"),sQuery(id+"F0.wireOp",EDGE,"E43.1"),sQuery(id+"F0.wireOp",EDGE,"E43.2"),sQuery(id+"F0.wireOp",EDGE,"E43.3"),sQuery(id+"F0.wireOp",EDGE,"E44.0"),sQuery(id+"F0.wireOp",EDGE,"E44.1"),sQuery(id+"F0.wireOp",EDGE,"E44.2"),sQuery(id+"F0.wireOp",EDGE,"E44.3"),sQuery(id+"F0.wireOp",EDGE,"E45.0"),sQuery(id+"F0.wireOp",EDGE,"E45.1"),sQuery(id+"F0.wireOp",EDGE,"E45.2"),sQuery(id+"F0.wireOp",EDGE,"E45.3"),sQuery(id+"F0.wireOp",EDGE,"E46.0"),sQuery(id+"F0.wireOp",EDGE,"E46.1"),sQuery(id+"F0.wireOp",EDGE,"E46.2"),sQuery(id+"F0.wireOp",EDGE,"E46.3"),sQuery(id+"F0.wireOp",EDGE,"E47.0"),sQuery(id+"F0.wireOp",EDGE,"E47.1"),sQuery(id+"F0.wireOp",EDGE,"E47.2"),sQuery(id+"F0.wireOp",EDGE,"E47.3"),sQuery(id+"F0.wireOp",EDGE,"E47.4"),sQuery(id+"F0.wireOp",EDGE,"E47.5"),sQuery(id+"F0.wireOp",EDGE,"E48.0"),sQuery(id+"F0.wireOp",EDGE,"E48.1"),sQuery(id+"F0.wireOp",EDGE,"E48.2"),sQuery(id+"F0.wireOp",EDGE,"E48.3"),sQuery(id+"F0.wireOp",EDGE,"E48.4"),sQuery(id+"F0.wireOp",EDGE,"E48.5"),sQuery(id+"F0.wireOp",EDGE,"E49.0"),sQuery(id+"F0.wireOp",EDGE,"E49.1"),sQuery(id+"F0.wireOp",EDGE,"E49.2"),sQuery(id+"F0.wireOp",EDGE,"E49.3"),sQuery(id+"F0.wireOp",EDGE,"E49.4"),sQuery(id+"F0.wireOp",EDGE,"E49.5"),sQuery(id+"F0.wireOp",EDGE,"E50.0"),sQuery(id+"F0.wireOp",EDGE,"E50.1"),sQuery(id+"F0.wireOp",EDGE,"E50.3"),sQuery(id+"F0.wireOp",EDGE,"E50.4"),sQuery(id+"F0.wireOp",EDGE,"E50.5"),sQuery(id+"F0.wireOp",EDGE,"E51.0"),sQuery(id+"F0.wireOp",EDGE,"E51.1"),sQuery(id+"F0.wireOp",EDGE,"E51.2"),sQuery(id+"F0.wireOp",EDGE,"E51.3"),sQuery(id+"F0.wireOp",EDGE,"E51.4"),sQuery(id+"F0.wireOp",EDGE,"E51.5"),sQuery(id+"F0.wireOp",EDGE,"E52.0"),sQuery(id+"F0.wireOp",EDGE,"E52.1"),sQuery(id+"F0.wireOp",EDGE,"E52.2"),sQuery(id+"F0.wireOp",EDGE,"E52.3"),sQuery(id+"F0.wireOp",EDGE,"E52.4"),sQuery(id+"F0.wireOp",EDGE,"E52.5"),sQuery(id+"F0.wireOp",EDGE,"E53.0"),sQuery(id+"F0.wireOp",EDGE,"E53.1"),sQuery(id+"F0.wireOp",EDGE,"E53.2"),sQuery(id+"F0.wireOp",EDGE,"E53.3"),sQuery(id+"F0.wireOp",EDGE,"E53.4"),sQuery(id+"F0.wireOp",EDGE,"E53.5"),sQuery(id+"F0.wireOp",EDGE,"E54.0"),sQuery(id+"F0.wireOp",EDGE,"E54.1"),sQuery(id+"F0.wireOp",EDGE,"E54.2"),sQuery(id+"F0.wireOp",EDGE,"E54.3"),sQuery(id+"F0.wireOp",EDGE,"E54.4"),sQuery(id+"F0.wireOp",EDGE,"E54.5"),sQuery(id+"F0.wireOp",EDGE,"E55.0"),sQuery(id+"F0.wireOp",EDGE,"E55.1"),sQuery(id+"F0.wireOp",EDGE,"E55.2"),sQuery(id+"F0.wireOp",EDGE,"E55.3"),sQuery(id+"F0.wireOp",EDGE,"E55.4"),sQuery(id+"F0.wireOp",EDGE,"E55.5"),sQuery(id+"F0.wireOp",EDGE,"E56.0"),sQuery(id+"F0.wireOp",EDGE,"E56.1"),sQuery(id+"F0.wireOp",EDGE,"E56.2"),sQuery(id+"F0.wireOp",EDGE,"E56.3"),sQuery(id+"F0.wireOp",EDGE,"E56.4"),sQuery(id+"F0.wireOp",EDGE,"E56.5"),sQuery(id+"F0.wireOp",EDGE,"E57.0"),sQuery(id+"F0.wireOp",EDGE,"E57.1"),sQuery(id+"F0.wireOp",EDGE,"E57.2"),sQuery(id+"F0.wireOp",EDGE,"E57.3"),sQuery(id+"F0.wireOp",EDGE,"E57.4"),sQuery(id+"F0.wireOp",EDGE,"E57.5"),sQuery(id+"F0.wireOp",EDGE,"E58.0"),sQuery(id+"F0.wireOp",EDGE,"E58.1"),sQuery(id+"F0.wireOp",EDGE,"E58.2"),sQuery(id+"F0.wireOp",EDGE,"E58.3"),sQuery(id+"F0.wireOp",EDGE,"E58.4"),sQuery(id+"F0.wireOp",EDGE,"E58.5"),sQuery(id+"F0.wireOp",EDGE,"E59.0"),sQuery(id+"F0.wireOp",EDGE,"E59.1"),sQuery(id+"F0.wireOp",EDGE,"E59.2"),sQuery(id+"F0.wireOp",EDGE,"E59.3"),sQuery(id+"F0.wireOp",EDGE,"E59.4"),sQuery(id+"F0.wireOp",EDGE,"E59.5"),sQuery(id+"F0.wireOp",EDGE,"E60.0"),sQuery(id+"F0.wireOp",EDGE,"E60.1"),sQuery(id+"F0.wireOp",EDGE,"E60.2"),sQuery(id+"F0.wireOp",EDGE,"E60.3"),sQuery(id+"F0.wireOp",EDGE,"E60.4"),sQuery(id+"F0.wireOp",EDGE,"E60.5"),sQuery(id+"F0.wireOp",EDGE,"E61.0"),sQuery(id+"F0.wireOp",EDGE,"E61.1"),sQuery(id+"F0.wireOp",EDGE,"E61.2"),sQuery(id+"F0.wireOp",EDGE,"E61.3"),sQuery(id+"F0.wireOp",EDGE,"E61.4"),sQuery(id+"F0.wireOp",EDGE,"E61.5"),sQuery(id+"F0.wireOp",EDGE,"E62.0"),sQuery(id+"F0.wireOp",EDGE,"E62.3"),sQuery(id+"F0.wireOp",EDGE,"E62.4"),sQuery(id+"F0.wireOp",EDGE,"E62.5"),sQuery(id+"F0.wireOp",EDGE,"E63.0"),sQuery(id+"F0.wireOp",EDGE,"E63.3"),sQuery(id+"F0.wireOp",EDGE,"E63.4"),sQuery(id+"F0.wireOp",EDGE,"E63.5"),sQuery(id+"F0.wireOp",EDGE,"E64.0"),sQuery(id+"F0.wireOp",EDGE,"E64.1"),sQuery(id+"F0.wireOp",EDGE,"E64.3"),sQuery(id+"F0.wireOp",EDGE,"E64.4"),sQuery(id+"F0.wireOp",EDGE,"E64.5"),sQuery(id+"F0.wireOp",EDGE,"E65.0"),sQuery(id+"F0.wireOp",EDGE,"E65.1"),sQuery(id+"F0.wireOp",EDGE,"E65.3"),sQuery(id+"F0.wireOp",EDGE,"E65.4"),sQuery(id+"F0.wireOp",EDGE,"E65.5"),sQuery(id+"F0.wireOp",EDGE,"E66.0"),sQuery(id+"F0.wireOp",EDGE,"E66.3"),sQuery(id+"F0.wireOp",EDGE,"E66.4"),sQuery(id+"F0.wireOp",EDGE,"E66.5"),sQuery(id+"F0.wireOp",EDGE,"E67.0"),sQuery(id+"F0.wireOp",EDGE,"E67.3"),sQuery(id+"F0.wireOp",EDGE,"E67.4"),sQuery(id+"F0.wireOp",EDGE,"E67.5"),sQuery(id+"F0.wireOp",EDGE,"E68.0"),sQuery(id+"F0.wireOp",EDGE,"E68.3"),sQuery(id+"F0.wireOp",EDGE,"E68.4"),sQuery(id+"F0.wireOp",EDGE,"E68.5"),sQuery(id+"F0.wireOp",EDGE,"E69.0"),sQuery(id+"F0.wireOp",EDGE,"E69.3"),sQuery(id+"F0.wireOp",EDGE,"E69.4"),sQuery(id+"F0.wireOp",EDGE,"E69.5"),sQuery(id+"F0.wireOp",EDGE,"E70.0"),sQuery(id+"F0.wireOp",EDGE,"E70.3"),sQuery(id+"F0.wireOp",EDGE,"E70.4"),sQuery(id+"F0.wireOp",EDGE,"E70.5"),sQuery(id+"F0.wireOp",EDGE,"E71.0"),sQuery(id+"F0.wireOp",EDGE,"E71.3"),sQuery(id+"F0.wireOp",EDGE,"E71.4"),sQuery(id+"F0.wireOp",EDGE,"E71.5"),sQuery(id+"F0.wireOp",EDGE,"E72.4"),sQuery(id+"F0.wireOp",EDGE,"E72.5"),sQuery(id+"F0.wireOp",EDGE,"E73.3"),sQuery(id+"F0.wireOp",EDGE,"E73.4"),sQuery(id+"F0.wireOp",EDGE,"E73.5"),sQuery(id+"F0.wireOp",EDGE,"E74.4"),sQuery(id+"F0.wireOp",EDGE,"E74.5"),sQuery(id+"F0.wireOp",EDGE,"E75"),sQuery(id+"F0.wireOp",EDGE,"E76")])],"isStart":true});
            var sketch = newSketch(context, id + "F11", { "sketchPlane" : qUnion([Q0])});
            skLineSegment(sketch, "E108", {"start": v(-261.97, -25.31) * mm, "end": v(-136.15, -25.31) * mm});
            skArc(sketch, "E109", {"start": v(-237.27, -5.54) * mm, "mid": v(-252.1, -12.34) * mm, "end": v(-261.97, -25.31) * mm});
            skArc(sketch, "E110", {"start": v(-207.1, -5.54) * mm, "mid": v(-222.18, -4.68) * mm, "end": v(-237.27, -5.54) * mm});
            skArc(sketch, "E111", {"start": v(-207.1, -5.54) * mm, "mid": v(-175.21, -8.2) * mm, "end": v(-143.22, -8.68) * mm});
            skArc(sketch, "E112", {"start": v(-143.22, -8.68) * mm, "mid": v(-141.02, -17.56) * mm, "end": v(-136.15, -25.31) * mm});
            skSolve(sketch);
        }
        {
            var Q0;
            Q0=makeQuery(id+"F5.boolean.opBoolean","INTERSECT",EDGE,{"derivedFrom":[makeQuery(id+"F1.opExtrude","SWEPT_FACE",FACE,{"disambiguationData":[OSD([sQuery(id+"F0.wireOp",EDGE,"E75")])]}),makeQuery(id+"F5.*.split.splitOp","SPLIT",FACE,{"derivedFrom":makeQuery(id+"F5.opExtrude","SWEPT_FACE",FACE,{"disambiguationData":[OSD([sQuery(id+"F4.wireOp",EDGE,"E91")])]}),"isFromBackBody":true})]});
            var Q1;
            Q1=makeQuery(id+"F5.boolean.opBoolean","INTERSECT",EDGE,{"derivedFrom":[makeQuery(id+"F1.opExtrude","SWEPT_FACE",FACE,{"disambiguationData":[OSD([sQuery(id+"F0.wireOp",EDGE,"E75")])]}),makeQuery(id+"F5.*.split.splitOp","SPLIT",FACE,{"derivedFrom":makeQuery(id+"F5.opExtrude","SWEPT_FACE",FACE,{"disambiguationData":[OSD([sQuery(id+"F4.wireOp",EDGE,"E91")])]})})]});
            var Q2;
            Q2=makeQuery(id+"F5.boolean.opBoolean","INTERSECT",EDGE,{"derivedFrom":[makeQuery(id+"F1.opExtrude","SWEPT_FACE",FACE,{"disambiguationData":[OSD([sQuery(id+"F0.wireOp",EDGE,"E75")])]}),makeQuery(id+"F5.*.split.splitOp","SPLIT",FACE,{"derivedFrom":makeQuery(id+"F5.opExtrude","SWEPT_FACE",FACE,{"disambiguationData":[OSD([sQuery(id+"F4.wireOp",EDGE,"E90")])]})})]});
            var Q3;
            Q3=makeQuery(id+"F5.boolean.opBoolean","INTERSECT",EDGE,{"derivedFrom":[makeQuery(id+"F1.opExtrude","SWEPT_FACE",FACE,{"disambiguationData":[OSD([sQuery(id+"F0.wireOp",EDGE,"E75")])]}),makeQuery(id+"F5.*.split.splitOp","SPLIT",FACE,{"derivedFrom":makeQuery(id+"F5.opExtrude","SWEPT_FACE",FACE,{"disambiguationData":[OSD([sQuery(id+"F4.wireOp",EDGE,"E90")])]}),"isFromBackBody":true})]});
            chamfer(context, id + "F12", {"entities" : qUnion([Q0, Q1, Q2, Q3]), "width" : 0.7 * mm, "tangentPropagation" : true});
        }
        {
            var Q0;
            {var subQ218=sQuery(id+"F11.wireOp",EDGE,"E110");Q0=makeQuery(id+"F11.imprint","IMPRINT",FACE,{"disambiguationData":[TD([[makeQuery(id+"F11.imprint","IMPRINT",EDGE,{"derivedFrom":subQ218}),1.0]])]});}
            var Q1;
            {var subQ6=sQuery(id+"F11.wireOp",EDGE,"E109");var subQ7=sQuery(id+"F11.wireOp",EDGE,"E108");var subQ8=makeQuery(id+"F11.imprint","INTERSECT",VERTEX,{"derivedFrom":[subQ7,subQ6]});Q1=makeQuery(id+"F11.imprint","IMPRINT",FACE,{"disambiguationData":[TD([[makeQuery(id+"F11.imprint","IMPRINT",EDGE,{"disambiguationData":[TD([[subQ8,-1.0]])],"derivedFrom":subQ7}),1.0]])]});}
            var Q2;
            Q2=sQuery(id+"F11.wireOp",EDGE,"E108");
            var Q3;
            Q3=sQuery(id+"F11.wireOp",EDGE,"E109");
            var Q4;
            Q4=sQuery(id+"F11.wireOp",EDGE,"E111");
            var Q5;
            Q5=sQuery(id+"F11.wireOp",EDGE,"E112");
            var Q6;
            Q6=sQuery(id+"F11.wireOp",EDGE,"E110");
            extrude(context, id + "F13", {"entities" : qUnion([Q0, Q1]), "operationType" : NewBodyOperationType.REMOVE, "surfaceEntities" : qUnion([Q2, Q3, Q4, Q5, Q6]), "oppositeDirection" : true, "depth" : 1 * mm});
        }
    });
